FCSTD DOCUMENT  (FreeCAD 0.19R22665 (Git))
Label: assembly
License: All rights reserved
LicenseURL: http://en.wikipedia.org/wiki/All_rights_reserved
objects: App::Link×5, App::DocumentObjectGroup×2, PartDesign::CoordinateSystem×1, App::FeaturePython×1, App::Part×1
note: 1 computed .brp shape members not serialized (recipe doc carries the construction recipe); baked Part::Feature solids carry a one-line shape summary decoded from their .brp
EXTERNAL_REF file=box_part.FCStd obj=LCS_backplane
EXTERNAL_REF file=box_part.FCStd obj=Body
EXTERNAL_REF file=box_part.FCStd obj=LCS_pcb
EXTERNAL_REF file=pcb_board.FCStd obj=LCS_box
EXTERNAL_REF file=pcb_board.FCStd obj=Board_8929
EXTERNAL_REF file=lcd.FCStd obj=LCS_pcb
EXTERNAL_REF file=pcb_board.FCStd obj=LCS_lcd
EXTERNAL_REF file=lcd.FCStd obj=Part
EXTERNAL_REF file=box_part.FCStd obj=LCS_coperchio
EXTERNAL_REF file=coperchio.FCStd obj=LCS_box
EXTERNAL_REF file=coperchio.FCStd obj=Part
EXTERNAL_REF file=coperchio.FCStd obj=LCS_button
EXTERNAL_REF file=push_button.FCStd obj=LCS_coperchio
EXTERNAL_REF file=push_button.FCStd obj=Part

FEATURE [App::DocumentObjectGroup] Parts
FEATURE [PartDesign::CoordinateSystem] LCS_Origin
  AttacherType = Attacher::AttachEngine3D
  MapMode = 2
  Support = -> [X_Axis]
FEATURE [App::DocumentObjectGroup] Constraints
FEATURE [App::FeaturePython] Variables  # WARN: FeaturePython — macro-defined, semantics opaque (R4)
FEATURE [App::Link] box_part_box
  AssemblyType = Asm4EE
  AttachedBy = #LCS_backplane
  AttachedTo = Parent Assembly#LCS_Origin
  AttachmentOffset = pos=(0,0,0) rot=(0,0.707107,0.707107;3.14159rad)
  LinkPlacement = pos=(1e-16,2,-4e-16) rot=(0,0,1;0rad)
  LinkedObject = -> <external box_part.FCStd>#Body
  Placement = pos=(1e-16,2,-4e-16) rot=(0,0,1;0rad)
  expr: Placement = LCS_Origin.Placement * AttachmentOffset * box_part#LCS_backplane.Placement ^ -1
FEATURE [App::Link] pcb_board_livello_serbatoio_definitiva
  AssemblyType = Asm4EE
  AttachedBy = #LCS_box
  AttachedTo = box_part_box#LCS_pcb
  LinkPlacement = pos=(-68.25,-39.4,154) rot=(1,0,0;1.5708rad)
  LinkedObject = -> <external pcb_board.FCStd>#Board_8929
  Placement = pos=(-68.25,-39.4,154) rot=(1,0,0;1.5708rad)
  expr: Placement = box_part_box.Placement * box_part#LCS_pcb.Placement * AttachmentOffset * pcb_board#LCS_box.Placement ^ -1
FEATURE [App::Link] lcd_lcd_block
  AssemblyType = Asm4EE
  AttachedBy = #LCS_pcb
  AttachedTo = pcb_board_livello_serbatoio_definitiva#LCS_lcd
  LinkPlacement = pos=(100.73,-48.9,32.02) rot=(1,0,0;1.5708rad)
  LinkedObject = -> <external lcd.FCStd>#Part
  Placement = pos=(100.73,-48.9,32.02) rot=(1,0,0;1.5708rad)
  expr: Placement = pcb_board_livello_serbatoio_definitiva.Placement * pcb_board#LCS_lcd.Placement * AttachmentOffset * lcd#LCS_pcb.Placement ^ -1
FEATURE [App::Link] coperchio_coperchio_completo
  AssemblyType = Asm4EE
  AttachedBy = #LCS_box
  AttachedTo = box_part_box#LCS_coperchio
  LinkPlacement = pos=(4e-15,-13,2.13e-14) rot=(0,0,1;0rad)
  LinkedObject = -> <external coperchio.FCStd>#Part
  Placement = pos=(4e-15,-13,2.13e-14) rot=(0,0,1;0rad)
  expr: Placement = box_part_box.Placement * box_part#LCS_coperchio.Placement * AttachmentOffset * coperchio#LCS_box.Placement ^ -1
FEATURE [App::Link] push_button_push_button_complete
  AssemblyType = Asm4EE
  AttachedBy = #LCS_coperchio
  AttachedTo = coperchio_coperchio_completo#LCS_button
  AttachmentOffset = pos=(0,0,0) rot=(-1,0,0;3.14159rad)
  LinkPlacement = pos=(121.75,-60,50) rot=(0,-1,0;3.14159rad)
  LinkedObject = -> <external push_button.FCStd>#Part
  Placement = pos=(121.75,-60,50) rot=(0,-1,0;3.14159rad)
  expr: Placement = coperchio_coperchio_completo.Placement * coperchio#LCS_button.Placement * AttachmentOffset * push_button#LCS_coperchio.Placement ^ -1
FEATURE [App::Part] Model
  Configuration = 0
  Group = -> [LCS_Origin,Constraints,Variables,box_part_box,pcb_board_livello_serbatoio_definitiva,lcd_lcd_block,coperchio_coperchio_completo,push_button_push_button_complete]
  Origin = -> Origin
  Type = Assembly4 Model

RESOLVED EXTERNAL PARTS (link-assembly join: the EXTERNAL_REF files above that resolve inside this repo's crawl, each included once):
---- part box_part.FCStd = doc fcstd_5c013ba1774b ----
FCSTD DOCUMENT  (FreeCAD 0.19R22665 (Git))
Label: box_part
License: All rights reserved
LicenseURL: http://en.wikipedia.org/wiki/All_rights_reserved
objects: Sketcher::SketchObject×9, PartDesign::Pocket×6, PartDesign::Pad×3, PartDesign::CoordinateSystem×3, PartDesign::Fillet×2, PartDesign::Chamfer×1, PartDesign::Body×1
note: 37 computed .brp shape members not serialized (recipe doc carries the construction recipe); baked Part::Feature solids carry a one-line shape summary decoded from their .brp

FEATURE [Sketcher::SketchObject] Sketch
  MapMode = 5
  Placement = pos=(0,0,0) rot=(1,0,0;1.5708rad)
  Support = -> [XZ_Plane]
  sketch-geometry (4):
    g0: LineSegment StartX=0 StartY=0 StartZ=0 EndX=150 EndY=0 EndZ=0
    g1: LineSegment StartX=150 StartY=0 StartZ=0 EndX=150 EndY=100 EndZ=0
    g2: LineSegment StartX=150 StartY=100 StartZ=0 EndX=0 EndY=100 EndZ=0
    g3: LineSegment StartX=0 StartY=100 StartZ=0 EndX=0 EndY=0 EndZ=0
  constraints (11):
    c: Coincident(g0,g1)
    c: Coincident(g1,g2)
    c: Coincident(g2,g3)
    c: Coincident(g3,g0)
    c: Horizontal(g0)
    c: Horizontal(g2)
    c: Vertical(g1)
    c: Vertical(g3)
    c: Coincident(g0,g-1)
    c: Distance(g2) = 150
    c: Distance(g3) = 100
FEATURE [PartDesign::Pad] Pad
  Direction = (1,1,1)
  Length = 60
  Length2 = 100
  Placement = pos=(0,0,0) rot=(1,0,0;1.5708rad)
  Profile = -> Sketch
  Type = 0
FEATURE [Sketcher::SketchObject] Sketch001
  ExternalGeometry = -> [Pad]
  MapMode = 5
  Placement = pos=(0,-60,-1.32e-14) rot=(1,0,0;1.5708rad)
  Support = -> [Pad]
  sketch-geometry (13):
    g0: LineSegment StartX=2 StartY=98 StartZ=0 EndX=148 EndY=98 EndZ=0
    g1: LineSegment StartX=148 StartY=98 StartZ=0 EndX=148 EndY=56 EndZ=0
    g2: LineSegment StartX=148 StartY=56 StartZ=0 EndX=142 EndY=56 EndZ=0
    g3: LineSegment StartX=142 StartY=56 StartZ=0 EndX=142 EndY=44 EndZ=0
    g4: LineSegment StartX=142 StartY=44 StartZ=0 EndX=148 EndY=44 EndZ=0
    g5: LineSegment StartX=148 StartY=44 StartZ=0 EndX=148 EndY=2 EndZ=0
    g6: LineSegment StartX=148 StartY=2 StartZ=0 EndX=2 EndY=2 EndZ=0
    g7: LineSegment StartX=2 StartY=2 StartZ=0 EndX=2 EndY=44 EndZ=0
    g8: LineSegment StartX=2 StartY=44 StartZ=0 EndX=8 EndY=44 EndZ=0
    g9: LineSegment StartX=8 StartY=44 StartZ=0 EndX=8 EndY=56 EndZ=0
    g10: LineSegment StartX=8 StartY=56 StartZ=0 EndX=2 EndY=56 EndZ=0
    g11: LineSegment StartX=2 StartY=56 StartZ=0 EndX=2 EndY=98 EndZ=0
    g12: LineSegment [constr] StartX=0 StartY=50 StartZ=0 EndX=150 EndY=50 EndZ=0
  constraints (37):
    c: Horizontal(g0)
    c: Coincident(g0,g1)
    c: Vertical(g1)
    c: Coincident(g1,g2)
    c: Horizontal(g2)
    c: Coincident(g2,g3)
    c: Vertical(g3)
    c: Coincident(g3,g4)
    c: Horizontal(g4)
    c: Coincident(g4,g5)
    c: Vertical(g5)
    c: Coincident(g5,g6)
    c: Horizontal(g6)
    c: Coincident(g6,g7)
    c: Vertical(g7)
    c: Coincident(g7,g8)
    c: Horizontal(g8)
    c: Coincident(g8,g9)
    c: Vertical(g9)
    c: Coincident(g9,g10)
    c: Horizontal(g10)
    c: Coincident(g10,g11)
    c: Coincident(g11,g0)
    c: Vertical(g11)
    c: DistanceX(g-1,g6) = 2
    c: DistanceY(g-1,g6) = 2
    c: DistanceX(g5,g-5) = 2
    c: DistanceY(g0,g-6) = 2
    c: PointOnObject(g12,g-4)
    c: PointOnObject(g12,g-5)
    c: Symmetric(g-6,g-1,g12)
    c: Symmetric(g10,g7,g12)
    c: DistanceX(g10,g10) = 6
    c: DistanceY(g9,g9) = 12
    c: Equal(g2,g10)
    c: Equal(g3,g9)
    c: Symmetric(g1,g4,g12)
FEATURE [PartDesign::Pocket] Pocket
  BaseFeature = -> Pad
  Length = 58
  Length2 = 100
  Placement = pos=(0,0,0) rot=(1,0,0;1.5708rad)
  Profile = -> Sketch001
  Type = 0
FEATURE [Sketcher::SketchObject] Sketch002
  ExternalGeometry = -> [Pocket]
  MapMode = 5
  Placement = pos=(0,-2,-4e-16) rot=(1,0,0;1.5708rad)
  Support = -> [Pocket]
  sketch-geometry (20):
    g0: LineSegment [constr] StartX=20.75 StartY=68 StartZ=0 EndX=100.75 EndY=68 EndZ=0
    g1: LineSegment [constr] StartX=100.75 StartY=68 StartZ=0 EndX=100.75 EndY=32 EndZ=0
    g2: LineSegment [constr] StartX=100.75 StartY=32 StartZ=0 EndX=20.75 EndY=32 EndZ=0
    g3: LineSegment [constr] StartX=20.75 StartY=32 StartZ=0 EndX=20.75 EndY=68 EndZ=0
    g4: LineSegment [constr] StartX=8 StartY=50 StartZ=0 EndX=142 EndY=50 EndZ=0
    g5: Circle [constr] CenterX=121.75 CenterY=50 CenterZ=0 NormalX=0 NormalY=0 NormalZ=1 AngleXU=0 Radius=9.5
    g6: LineSegment [constr] StartX=101.75 StartY=14 StartZ=0 EndX=18.75 EndY=14 EndZ=0
    g7: LineSegment [constr] StartX=18.75 StartY=14 StartZ=0 EndX=18.75 EndY=86 EndZ=0
    g8: LineSegment [constr] StartX=18.75 StartY=86 StartZ=0 EndX=101.75 EndY=86 EndZ=0
    g9: LineSegment [constr] StartX=101.75 StartY=86 StartZ=0 EndX=101.75 EndY=14 EndZ=0
    g10: LineSegment [constr] StartX=101.75 StartY=59 StartZ=0 EndX=107.75 EndY=59 EndZ=0
    g11: LineSegment [constr] StartX=107.75 StartY=59 StartZ=0 EndX=107.75 EndY=72 EndZ=0
    g12: LineSegment [constr] StartX=107.75 StartY=72 StartZ=0 EndX=101.75 EndY=72 EndZ=0
    g13: LineSegment [constr] StartX=101.75 StartY=72 StartZ=0 EndX=101.75 EndY=59 EndZ=0
    g14: Circle [constr] CenterX=13.375 CenterY=50 CenterZ=0 NormalX=0 NormalY=0 NormalZ=1 AngleXU=0 Radius=5.375
    g15: Circle [constr] CenterX=136.625 CenterY=50 CenterZ=0 NormalX=0 NormalY=0 NormalZ=1 AngleXU=0 Radius=5.375
    g16: Circle CenterX=24.75 CenterY=80 CenterZ=0 NormalX=0 NormalY=0 NormalZ=1 AngleXU=0 Radius=3
    g17: Circle CenterX=95.75 CenterY=80 CenterZ=0 NormalX=0 NormalY=0 NormalZ=1 AngleXU=0 Radius=3
    g18: Circle CenterX=24.75 CenterY=20 CenterZ=0 NormalX=0 NormalY=0 NormalZ=1 AngleXU=0 Radius=3
    g19: Circle CenterX=95.75 CenterY=20 CenterZ=0 NormalX=0 NormalY=0 NormalZ=1 AngleXU=0 Radius=3
  constraints (59):
    c: Coincident(g0,g1)
    c: Coincident(g1,g2)
    c: Coincident(g2,g3)
    c: Coincident(g3,g0)
    c: Horizontal(g0)
    c: Horizontal(g2)
    c: Vertical(g1)
    c: DistanceY(g3,g3) = 36
    c: DistanceX(g0,g0) = 80
    c: PointOnObject(g4,g-13)
    c: PointOnObject(g4,g-11)
    c: Symmetric(g-13,g-14,g4)
    c: Symmetric(g0,g2,g4)
    c: PointOnObject(g5,g4)
    c: Diameter(g5) = 19
    c: Coincident(g6,g7)
    c: Coincident(g7,g8)
    c: Coincident(g8,g9)
    c: Coincident(g9,g6)
    c: Horizontal(g6)
    c: Horizontal(g8)
    c: Vertical(g7)
    c: Vertical(g9)
    c: DistanceX(g6,g2) = 2
    c: DistanceY(g0,g7) = 18
    c: DistanceY(g6,g2) = 18
    c: DistanceX(g8,g8) = 83
    c: Coincident(g10,g11)
    c: Coincident(g11,g12)
    c: Coincident(g12,g13)
    c: Coincident(g13,g10)
    c: Horizontal(g10)
    c: Horizontal(g12)
    c: Vertical(g11)
    c: Vertical(g13)
    c: PointOnObject(g10,g9)
    c: DistanceY(g11,g11) = 13
    c: DistanceY(g12,g8) = 14
    c: DistanceX(g12,g12) = 6
    c: DistanceX(g6,g5) = 20
    c: PointOnObject(g14,g4)
    c: PointOnObject(g4,g14)
    c: Tangent(g14,g7)
    c: PointOnObject(g15,g4)
    c: PointOnObject(g4,g15)
    c: Tangent(g15,g5)
    c: Equal(g15,g14)
    c: DistanceX(g7,g16) = 6
    c: DistanceY(g16,g7) = 6
    c: Diameter(g16) = 6
    c: Horizontal(g17,g16)
    c: Equal(g17,g16)
    c: DistanceX(g17,g8) = 6
    c: Equal(g18,g16)
    c: Vertical(g16,g18)
    c: DistanceY(g6,g18) = 6
    c: Equal(g19,g16)
    c: Horizontal(g19,g18)
    c: Vertical(g17,g19)
FEATURE [PartDesign::Pad] Pad001
  BaseFeature = -> Pocket
  Direction = (1,1,1)
  Length = 37.8
  Length2 = 100
  Placement = pos=(0,0,0) rot=(1,0,0;1.5708rad)
  Profile = -> Sketch002
  Type = 0
FEATURE [Sketcher::SketchObject] Sketch005
  MapMode = 5
  Placement = pos=(0,0,0) rot=(1,0,0;3.14159rad)
  sketch-geometry (5):
    g0: LineSegment [constr] StartX=75 StartY=60 StartZ=0 EndX=75 EndY=0 EndZ=0
    g1: ArcOfCircle CenterX=65 CenterY=9 CenterZ=0 NormalX=0 NormalY=0 NormalZ=1 AngleXU=0 Radius=4 StartAngle=1.5708 EndAngle=4.71239
    g2: ArcOfCircle CenterX=85 CenterY=9 CenterZ=0 NormalX=0 NormalY=0 NormalZ=1 AngleXU=0 Radius=4 StartAngle=4.71239 EndAngle=7.85398
    g3: LineSegment StartX=65 StartY=5 StartZ=0 EndX=85 EndY=5 EndZ=0
    g4: LineSegment StartX=65 StartY=13 StartZ=0 EndX=85 EndY=13 EndZ=0
  constraints (9):
    c: Tangent(g1,g4)
    c: Tangent(g1,g3)
    c: Tangent(g3,g2)
    c: Tangent(g4,g2)
    c: Horizontal(g3)
    c: DistanceX(g1,g2) = 20
    c: DistanceY(g1,g1) = 8
    c: Symmetric(g2,g1,g0)
    c: DistanceY(g0,g2) = 5
FEATURE [PartDesign::Pocket] Pocket001
  BaseFeature = -> Pad001
  Length = 5
  Length2 = 100
  Placement = pos=(0,0,0) rot=(1,0,0;1.5708rad)
  Profile = -> Sketch005
  Type = 2
FEATURE [Sketcher::SketchObject] Sketch006
  ExternalGeometry = -> [Pocket001]
  MapMode = 5
  Placement = pos=(150,0,0) rot=(0.707107,0,0.707107;3.14159rad)
  Support = -> [Pocket001]
  sketch-geometry (5):
    g0: LineSegment [constr] StartX=0 StartY=30 StartZ=0 EndX=2 EndY=30 EndZ=0
    g1: ArcOfCircle CenterX=17.5 CenterY=35 CenterZ=0 NormalX=0 NormalY=0 NormalZ=1 AngleXU=0 Radius=7.5 StartAngle=1e-16 EndAngle=3.14159
    g2: ArcOfCircle CenterX=17.5 CenterY=25 CenterZ=0 NormalX=0 NormalY=0 NormalZ=1 AngleXU=0 Radius=7.5 StartAngle=3.14159 EndAngle=6.28319
    g3: LineSegment StartX=10 StartY=35 StartZ=0 EndX=10 EndY=25 EndZ=0
    g4: LineSegment StartX=25 StartY=35 StartZ=0 EndX=25 EndY=25 EndZ=0
  constraints (12):
    c: PointOnObject(g0,g-6)
    c: PointOnObject(g0,g-4)
    c: Symmetric(g-6,g-1,g0)
    c: Tangent(g1,g4)
    c: Tangent(g1,g3)
    c: Tangent(g3,g2)
    c: Tangent(g4,g2)
    c: Vertical(g3)
    c: Symmetric(g1,g2,g0)
    c: DistanceX(g1,g1) = 15
    c: Distance(g1,g2) = 10
    c: DistanceX(g-6,g1) = 10
FEATURE [PartDesign::Pocket] Pocket002
  BaseFeature = -> Pocket001
  Length = 5
  Length2 = 100
  Placement = pos=(0,0,0) rot=(1,0,0;1.5708rad)
  Profile = -> Sketch006
  Type = 2
FEATURE [Sketcher::SketchObject] Sketch007
  ExternalGeometry = -> [Pocket002]
  MapMode = 5
  Placement = pos=(0,-2,-4e-16) rot=(1,0,0;1.5708rad)
  Support = -> [Pocket002]
  sketch-geometry (4):
    g0: Circle CenterX=40 CenterY=50 CenterZ=0 NormalX=0 NormalY=0 NormalZ=1 AngleXU=0 Radius=1
    g1: Circle CenterX=110 CenterY=50 CenterZ=0 NormalX=0 NormalY=0 NormalZ=1 AngleXU=0 Radius=1
    g2: LineSegment [constr] StartX=8 StartY=50 StartZ=0 EndX=142 EndY=50 EndZ=0
    g3: LineSegment [constr] StartX=75 StartY=98 StartZ=0 EndX=75 EndY=2 EndZ=0
  constraints (11):
    c: Diameter(g0) = 2
    c: Equal(g1,g0)
    c: DistanceX(g0,g1) = 70
    c: PointOnObject(g2,g-3)
    c: PointOnObject(g2,g-4)
    c: Symmetric(g-4,g-4,g2)
    c: PointOnObject(g0,g2)
    c: PointOnObject(g3,g-5)
    c: PointOnObject(g3,g-6)
    c: Symmetric(g-5,g-5,g3)
    c: Symmetric(g0,g1,g3)
FEATURE [PartDesign::Pocket] Pocket003
  BaseFeature = -> Pocket002
  Length = 2
  Length2 = 100
  Placement = pos=(0,0,0) rot=(1,0,0;1.5708rad)
  Profile = -> Sketch007
  Type = 1
FEATURE [Sketcher::SketchObject] Sketch009
  ExternalGeometry = -> [Pocket003]
  MapMode = 5
  Placement = pos=(-2e-15,-39.8,-1.03e-14) rot=(1,0,0;1.5708rad)
  Support = -> [Pocket003]
  sketch-geometry (4):
    g0: Circle CenterX=24.75 CenterY=80 CenterZ=0 NormalX=0 NormalY=0 NormalZ=1 AngleXU=0 Radius=1.5
    g1: Circle CenterX=95.75 CenterY=80 CenterZ=0 NormalX=0 NormalY=0 NormalZ=1 AngleXU=0 Radius=1.5
    g2: Circle CenterX=24.75 CenterY=20 CenterZ=0 NormalX=0 NormalY=0 NormalZ=1 AngleXU=0 Radius=1.5
    g3: Circle CenterX=95.75 CenterY=20 CenterZ=0 NormalX=0 NormalY=0 NormalZ=1 AngleXU=0 Radius=1.5
  constraints (8):
    c: Coincident(g0,g-3)
    c: Coincident(g1,g-4)
    c: Coincident(g2,g-6)
    c: Coincident(g3,g-5)
    c: Diameter(g0) = 3
    c: Equal(g1,g0)
    c: Equal(g2,g0)
    c: Equal(g2,g3)
FEATURE [PartDesign::Pad] Pad003
  BaseFeature = -> Pocket003
  Direction = (1,1,1)
  Length = 10
  Length2 = 100
  Placement = pos=(0,0,0) rot=(1,0,0;1.5708rad)
  Profile = -> Sketch009
  Type = 0
FEATURE [Sketcher::SketchObject] Sketch010
  ExternalGeometry = -> [Pad003]
  MapMode = 5
  Placement = pos=(0,-1.85e-14,56) rot=(0,0,1;3.14159rad)
  Support = -> [Pad003]
  sketch-geometry (18):
    g0: LineSegment StartX=-3.75 StartY=60 StartZ=0 EndX=-3.75 EndY=57.3 EndZ=0
    g1: LineSegment StartX=-3.75 StartY=57.3 StartZ=0 EndX=-2.75 EndY=57.3 EndZ=0
    g2: LineSegment StartX=-2.75 StartY=57.3 StartZ=0 EndX=-2.75 EndY=51.7 EndZ=0
    g3: LineSegment StartX=-2.75 StartY=51.7 StartZ=0 EndX=-7.25 EndY=51.7 EndZ=0
    g4: LineSegment StartX=-7.25 StartY=51.7 StartZ=0 EndX=-7.25 EndY=57.3 EndZ=0
    g5: LineSegment StartX=-7.25 StartY=57.3 StartZ=0 EndX=-6.25 EndY=57.3 EndZ=0
    g6: LineSegment StartX=-6.25 StartY=57.3 StartZ=0 EndX=-6.25 EndY=60 EndZ=0
    g7: LineSegment StartX=-6.25 StartY=60 StartZ=0 EndX=-3.75 EndY=60 EndZ=0
    g8: LineSegment [constr] StartX=-2 StartY=50 StartZ=0 EndX=-8 EndY=50 EndZ=0
    g9: LineSegment [constr] StartX=-5 StartY=50 StartZ=0 EndX=-5 EndY=60 EndZ=0
    g10: LineSegment [constr] StartX=-6 StartY=60 StartZ=0 EndX=-4 EndY=60 EndZ=0
    g11: LineSegment [constr] StartX=-4 StartY=60 StartZ=0 EndX=-4 EndY=52 EndZ=0
    g12: LineSegment [constr] StartX=-4 StartY=52 StartZ=0 EndX=-6 EndY=52 EndZ=0
    g13: LineSegment [constr] StartX=-6 StartY=52 StartZ=0 EndX=-6 EndY=60 EndZ=0
    g14: LineSegment [constr] StartX=-7 StartY=52 StartZ=0 EndX=-3 EndY=52 EndZ=0
    g15: LineSegment [constr] StartX=-3 StartY=52 StartZ=0 EndX=-3 EndY=57 EndZ=0
    g16: LineSegment [constr] StartX=-3 StartY=57 StartZ=0 EndX=-7 EndY=57 EndZ=0
    g17: LineSegment [constr] StartX=-7 StartY=57 StartZ=0 EndX=-7 EndY=52 EndZ=0
  constraints (52):
    c: PointOnObject(g0,g-3)
    c: Vertical(g0)
    c: Coincident(g0,g1)
    c: Coincident(g1,g2)
    c: Vertical(g2)
    c: Coincident(g2,g3)
    c: Horizontal(g3)
    c: Coincident(g3,g4)
    c: Vertical(g4)
    c: Coincident(g4,g5)
    c: Horizontal(g5)
    c: Coincident(g5,g6)
    c: PointOnObject(g6,g-3)
    c: Vertical(g6)
    c: Coincident(g6,g7)
    c: Coincident(g7,g0)
    c: DistanceX(g6,g0) = 2.5
    c: DistanceX(g1,g1) = 1
    c: DistanceY(g4,g4) = 5.6
    c: Horizontal(g1)
    c: DistanceY(g6,g6) = 2.7
    c: PointOnObject(g8,g-5)
    c: Horizontal(g8)
    c: PointOnObject(g9,g8)
    c: Symmetric(g-5,g-4,g9)
    c: Symmetric(g0,g5,g9)
    c: DistanceY(g8,g-4) = 10
    c: PointOnObject(g9,g7)
    c: PointOnObject(g8,g-4)
    c: Equal(g1,g5)
    c: Coincident(g10,g11)
    c: Coincident(g11,g12)
    c: Coincident(g12,g13)
    c: Coincident(g13,g10)
    c: Horizontal(g12)
    c: Vertical(g11)
    c: Vertical(g13)
    c: PointOnObject(g10,g7)
    c: Symmetric(g10,g10,g9)
    c: DistanceX(g12,g12) = 2
    c: DistanceY(g13,g13) = 8
    c: Coincident(g14,g15)
    c: Coincident(g15,g16)
    c: Coincident(g16,g17)
    c: Coincident(g17,g14)
    c: Horizontal(g14)
    c: Vertical(g15)
    c: Vertical(g17)
    c: DistanceX(g16,g16) = 4
    c: Symmetric(g15,g16,g9)
    c: DistanceY(g15,g10) = 3
    c: DistanceY(g11,g14) = 0
FEATURE [PartDesign::Pocket] Pocket004
  BaseFeature = -> Pad003
  Length = 6
  Length2 = 100
  Placement = pos=(0,0,0) rot=(1,0,0;1.5708rad)
  Profile = -> Sketch010
  Type = 0
FEATURE [Sketcher::SketchObject] Sketch011
  ExternalGeometry = -> [Pocket004]
  MapMode = 5
  Placement = pos=(0,-1.85e-14,56) rot=(0,0,1;3.14159rad)
  Support = -> [Pocket004]
  sketch-geometry (9):
    g0: LineSegment StartX=-143.75 StartY=60 StartZ=0 EndX=-146.25 EndY=60 EndZ=0
    g1: LineSegment StartX=-146.25 StartY=60 StartZ=0 EndX=-146.25 EndY=57.3 EndZ=0
    g2: LineSegment StartX=-146.25 StartY=57.3 StartZ=0 EndX=-147.25 EndY=57.3 EndZ=0
    g3: LineSegment StartX=-147.25 StartY=57.3 StartZ=0 EndX=-147.25 EndY=51.7 EndZ=0
    g4: LineSegment StartX=-147.25 StartY=51.7 StartZ=0 EndX=-142.75 EndY=51.7 EndZ=0
    g5: LineSegment StartX=-142.75 StartY=51.7 StartZ=0 EndX=-142.75 EndY=57.3 EndZ=0
    g6: LineSegment StartX=-142.75 StartY=57.3 StartZ=0 EndX=-143.75 EndY=57.3 EndZ=0
    g7: LineSegment StartX=-143.75 StartY=57.3 StartZ=0 EndX=-143.75 EndY=60 EndZ=0
    g8: LineSegment [constr] StartX=-145 StartY=51.7 StartZ=0 EndX=-145 EndY=60 EndZ=0
  constraints (26):
    c: PointOnObject(g0,g-3)
    c: PointOnObject(g0,g-3)
    c: Coincident(g0,g1)
    c: Vertical(g1)
    c: Coincident(g1,g2)
    c: Coincident(g2,g3)
    c: Vertical(g3)
    c: Coincident(g3,g4)
    c: Horizontal(g4)
    c: Coincident(g4,g5)
    c: Coincident(g5,g6)
    c: Coincident(g6,g7)
    c: Coincident(g7,g0)
    c: Equal(g5,g3)
    c: Equal(g2,g6)
    c: Equal(g7,g1)
    c: Vertical(g7)
    c: DistanceX(g0,g0) = 2.5
    c: Horizontal(g6)
    c: DistanceX(g6,g6) = 1
    c: DistanceY(g7,g7) = 2.7
    c: DistanceY(g5,g5) = 5.6
    c: PointOnObject(g8,g4)
    c: PointOnObject(g8,g0)
    c: Symmetric(g-4,g-5,g8)
    c: Symmetric(g5,g2,g8)
FEATURE [PartDesign::Pocket] Pocket005
  BaseFeature = -> Pocket004
  Length = 6
  Length2 = 100
  Placement = pos=(0,0,0) rot=(1,0,0;1.5708rad)
  Profile = -> Sketch011
  Type = 0
FEATURE [PartDesign::Chamfer] Chamfer
  Angle = 60
  Base = -> Pocket005 [Edge120,Edge122,Edge121,Edge119]
  BaseFeature = -> Pocket005
  ChamferType = 2
  FlipDirection = false
  Placement = pos=(0,0,0) rot=(1,0,0;1.5708rad)
  Size = 4
  Size2 = 1
  SupportTransform = false
FEATURE [PartDesign::Fillet] Fillet
  Base = -> Chamfer [Edge21,Edge56,Edge59,Edge23]
  BaseFeature = -> Chamfer
  Placement = pos=(0,0,0) rot=(1,0,0;1.5708rad)
  Radius = 2
  SupportTransform = false
FEATURE [PartDesign::Fillet] Fillet001
  Base = -> Fillet [Edge155,Edge157,Edge158,Edge156]
  BaseFeature = -> Fillet
  Placement = pos=(0,0,0) rot=(1,0,0;1.5708rad)
  Radius = 2
  SupportTransform = false
FEATURE [PartDesign::CoordinateSystem] LCS_backplane
  AttacherType = Attacher::AttachEngine3D
  MapMode = 5
  Placement = pos=(0,-2,-4e-16) rot=(0,0.707107,0.707107;3.14159rad)
  Support = -> [Fillet001]
FEATURE [PartDesign::CoordinateSystem] LCS_pcb
  AttacherType = Attacher::AttachEngine3D
  MapMode = 11
  Placement = pos=(24.75,-39.8,20) rot=(0.57735,-0.57735,0.57735;2.0944rad)
  Support = -> [Fillet001]
FEATURE [PartDesign::CoordinateSystem] LCS_coperchio
  AttacherType = Attacher::AttachEngine3D
  AttachmentOffset = pos=(0.3,0,-0.25) rot=(0,0,1;0rad)
  MapMode = 7
  Placement = pos=(3,-52,50) rot=(0.57735,-0.57735,-0.57735;2.0944rad)
  Support = -> [Fillet001]
FEATURE [PartDesign::Body] Body  label="box"
  Group = -> [Sketch,Pad,Sketch001,Pocket,Sketch002,Pad001,Sketch005,Pocket001,Sketch006,Pocket002,Sketch007,LCS_backplane,LCS_pcb,LCS_coperchio,Pocket003,Sketch009,Pad003,Sketch010,Pocket004,Sketch011,Pocket005,Chamfer,Fillet,Fillet001]
  Origin = -> Origin
  Tip = -> Fillet001
---- part coperchio.FCStd = doc fcstd_1bf6bf9a385b ----
FCSTD DOCUMENT  (FreeCAD 0.19R22665 (Git))
Label: coperchio
License: All rights reserved
LicenseURL: http://en.wikipedia.org/wiki/All_rights_reserved
objects: Sketcher::SketchObject×7, PartDesign::Pocket×5, PartDesign::Pad×3, PartDesign::CoordinateSystem×2, PartDesign::Body×2, Part::Fillet×2, Part::Part2DObjectPython×1, Part::Extrusion×1, Part::MultiFuse×1, App::Part×1
note: 32 computed .brp shape members not serialized (recipe doc carries the construction recipe); baked Part::Feature solids carry a one-line shape summary decoded from their .brp

FEATURE [Part::Part2DObjectPython] ShapeString  # Draft 2D object (typed FeaturePython)
  FontFile = <path>
  Placement = pos=(111.263,-47,22.0884) rot=(1,0,0;1.5708rad)
  Size = 2
  String = by GR 2021
  Tracking = 0
FEATURE [Part::Extrusion] Extrude002
  Base = -> ShapeString
  Dir = (0,-1,2e-16)
  DirMode = 2
  FaceMakerClass = Part::FaceMakerBullseye
  LengthFwd = 1
  LengthRev = 0
  Placement = pos=(21,0,-19) rot=(0,0,1;0rad)
  Solid = false
  Symmetric = false
FEATURE [Sketcher::SketchObject] Sketch008
  MapMode = 5
  Placement = pos=(0,-45,1e-16) rot=(1,0,0;1.5708rad)
  sketch-geometry (4):
    g0: LineSegment StartX=0 StartY=0 StartZ=0 EndX=150 EndY=0 EndZ=0
    g1: LineSegment StartX=150 StartY=0 StartZ=0 EndX=150 EndY=100 EndZ=0
    g2: LineSegment StartX=150 StartY=100 StartZ=0 EndX=0 EndY=100 EndZ=0
    g3: LineSegment StartX=0 StartY=100 StartZ=0 EndX=0 EndY=0 EndZ=0
  constraints (11):
    c: Coincident(g0,g1)
    c: Coincident(g1,g2)
    c: Coincident(g2,g3)
    c: Coincident(g3,g0)
    c: Horizontal(g0)
    c: Horizontal(g2)
    c: Vertical(g1)
    c: Vertical(g3)
    c: Coincident(g0,g-1)
    c: DistanceY(g0,g2) = 100
    c: DistanceX(g0,g0) = 150
FEATURE [PartDesign::Pad] Pad002
  Direction = (1,1,1)
  Length = 2
  Length2 = 100
  Placement = pos=(0,-45,1e-16) rot=(1,0,0;1.5708rad)
  Profile = -> Sketch008
  Type = 0
FEATURE [Sketcher::SketchObject] Sketch009
  ExternalGeometry = -> [Pad002]
  MapMode = 5
  Placement = pos=(0,-47,5e-16) rot=(1,0,0;1.5708rad)
  Support = -> [Pad002]
  sketch-geometry (22):
    g0: LineSegment StartX=23.75 StartY=64 StartZ=0 EndX=97.75 EndY=64 EndZ=0
    g1: LineSegment StartX=97.75 StartY=64 StartZ=0 EndX=97.75 EndY=36 EndZ=0
    g2: LineSegment StartX=97.75 StartY=36 StartZ=0 EndX=23.75 EndY=36 EndZ=0
    g3: LineSegment StartX=23.75 StartY=36 StartZ=0 EndX=23.75 EndY=64 EndZ=0
    g4: LineSegment [constr] StartX=18.75 StartY=86 StartZ=0 EndX=101.75 EndY=86 EndZ=0
    g5: LineSegment [constr] StartX=101.75 StartY=86 StartZ=0 EndX=101.75 EndY=14 EndZ=0
    g6: LineSegment [constr] StartX=101.75 StartY=14 StartZ=0 EndX=18.75 EndY=14 EndZ=0
    g7: LineSegment [constr] StartX=18.75 StartY=14 StartZ=0 EndX=18.75 EndY=86 EndZ=0
    g8: Circle CenterX=121.75 CenterY=50 CenterZ=0 NormalX=0 NormalY=0 NormalZ=1 AngleXU=0 Radius=9.5
    g9: LineSegment [constr] StartX=20.75 StartY=68 StartZ=0 EndX=100.75 EndY=68 EndZ=0
    g10: LineSegment [constr] StartX=100.75 StartY=68 StartZ=0 EndX=100.75 EndY=32 EndZ=0
    g11: LineSegment [constr] StartX=100.75 StartY=32 StartZ=0 EndX=20.75 EndY=32 EndZ=0
    g12: LineSegment [constr] StartX=20.75 StartY=32 StartZ=0 EndX=20.75 EndY=68 EndZ=0
    g13: LineSegment [constr] StartX=0 StartY=50 StartZ=0 EndX=150 EndY=50 EndZ=0
    g14: LineSegment [constr] StartX=60.75 StartY=68 StartZ=0 EndX=60.75 EndY=32 EndZ=0
    g15: Circle [constr] CenterX=9.375 CenterY=50 CenterZ=0 NormalX=0 NormalY=0 NormalZ=1 AngleXU=0 Radius=9.375
    g16: Circle [constr] CenterX=140.625 CenterY=50 CenterZ=0 NormalX=0 NormalY=0 NormalZ=1 AngleXU=0 Radius=9.375
    g17: ArcOfCircle CenterX=68.1 CenterY=80.85 CenterZ=0 NormalX=0 NormalY=0 NormalZ=1 AngleXU=0 Radius=3.25 StartAngle=1.5708 EndAngle=4.71239
    g18: ArcOfCircle CenterX=81.6 CenterY=80.85 CenterZ=0 NormalX=0 NormalY=0 NormalZ=1 AngleXU=0 Radius=3.25 StartAngle=4.71239 EndAngle=7.85398
    g19: LineSegment StartX=68.1 StartY=77.6 StartZ=0 EndX=81.6 EndY=77.6 EndZ=0
    g20: LineSegment StartX=68.1 StartY=84.1 StartZ=0 EndX=81.6 EndY=84.1 EndZ=0
    g21: LineSegment [constr] StartX=64.85 StartY=80.85 StartZ=0 EndX=84.85 EndY=80.85 EndZ=0
  constraints (61):
    c: Coincident(g0,g1)
    c: Coincident(g1,g2)
    c: Coincident(g2,g3)
    c: Coincident(g3,g0)
    c: Horizontal(g0)
    c: Horizontal(g2)
    c: Vertical(g1)
    c: Coincident(g4,g5)
    c: Coincident(g5,g6)
    c: Coincident(g6,g7)
    c: Coincident(g7,g4)
    c: Horizontal(g4)
    c: Horizontal(g6)
    c: Vertical(g5)
    c: Diameter(g8) = 19
    c: DistanceX(g4,g4) = 83
    c: Coincident(g9,g10)
    c: Coincident(g10,g11)
    c: Coincident(g11,g12)
    c: Coincident(g12,g9)
    c: Horizontal(g11)
    c: Vertical(g10)
    c: Vertical(g12)
    c: DistanceX(g9,g9) = 80
    c: DistanceX(g6,g11) = 2
    c: DistanceY(g9,g4) = 18
    c: DistanceY(g6,g11) = 18
    c: DistanceY(g12,g12) = 36
    c: PointOnObject(g13,g-3)
    c: PointOnObject(g13,g-6)
    c: Symmetric(g-4,g-1,g13)
    c: Symmetric(g4,g6,g13)
    c: PointOnObject(g8,g13)
    c: Symmetric(g0,g2,g13)
    c: PointOnObject(g14,g9)
    c: PointOnObject(g14,g11)
    c: Symmetric(g9,g9,g14)
    c: Symmetric(g0,g0,g14)
    c: Distance(g0) = 74
    c: Distance(g3) = 28
    c: Distance(g8,g5) = 20
    c: PointOnObject(g15,g13)
    c: PointOnObject(g13,g15)
    c: Tangent(g15,g7)
    c: PointOnObject(g16,g13)
    c: PointOnObject(g13,g16)
    c: Tangent(g16,g8)
    c: Equal(g16,g15)
    c: Tangent(g17,g20)
    c: Tangent(g17,g19)
    c: Tangent(g19,g18)
    c: Tangent(g20,g18)
    c: Horizontal(g19)
    c: Equal(g17,g18)
    c: DistanceY(g9,g18) = 9.6
    c: DistanceY(g18,g18) = 6.5
    c: PointOnObject(g21,g17)
    c: PointOnObject(g21,g18)
    c: Symmetric(g17,g17,g21)
    c: Distance(g21,g21) = 20
    c: DistanceX(g21,g9) = 15.9
FEATURE [PartDesign::Pocket] Pocket004
  BaseFeature = -> Pad002
  Length = 5
  Length2 = 100
  Placement = pos=(0,-45,1e-16) rot=(1,0,0;1.5708rad)
  Profile = -> Sketch009
  Type = 2
FEATURE [Sketcher::SketchObject] Sketch012
  MapMode = 5
  Placement = pos=(97.75,-45,0) rot=(0.707107,0,-0.707107;3.14159rad)
  sketch-geometry (5):
    g0: LineSegment StartX=-41 StartY=-1.54e-14 StartZ=0 EndX=-59 EndY=-1.54e-14 EndZ=0
    g1: LineSegment StartX=-59 StartY=-1.54e-14 StartZ=0 EndX=-59 EndY=1 EndZ=0
    g2: LineSegment StartX=-59 StartY=1 StartZ=0 EndX=-41 EndY=1 EndZ=0
    g3: LineSegment StartX=-41 StartY=1 StartZ=0 EndX=-41 EndY=-1.54e-14 EndZ=0
    g4: LineSegment [constr] StartX=-50 StartY=2 StartZ=0 EndX=-50 EndY=-1.55e-14 EndZ=0
  constraints (11):
    c: Coincident(g0,g1)
    c: Coincident(g1,g2)
    c: Coincident(g2,g3)
    c: Coincident(g3,g0)
    c: Horizontal(g0)
    c: Vertical(g1)
    c: Vertical(g3)
    c: Symmetric(g1,g2,g4)
    c: DistanceY(g1,g1) = 1
    c: DistanceX(g2,g2) = 18
    c: PointOnObject(g4,g0)
FEATURE [PartDesign::Pocket] Pocket007
  BaseFeature = -> Pocket004
  Length = 6
  Length2 = 100
  Placement = pos=(0,-45,1e-16) rot=(1,0,0;1.5708rad)
  Profile = -> Sketch012
  Type = 0
FEATURE [PartDesign::CoordinateSystem] LCS_button
  AttacherType = Attacher::AttachEngine3D
  MapMode = 11
  Placement = pos=(121.75,-47,50) rot=(0.57735,-0.57735,0.57735;2.0944rad)
  Support = -> [Pocket007]
FEATURE [Sketcher::SketchObject] Sketch
  ExternalGeometry = -> [Pocket007]
  MapMode = 5
  Placement = pos=(0,-45,1e-16) rot=(-1,0,0;1.5708rad)
  Support = -> [Pocket007]
  sketch-geometry (9):
    g0: LineSegment StartX=2 StartY=-50 StartZ=0 EndX=8 EndY=-50 EndZ=0
    g1: LineSegment StartX=8 StartY=-50 StartZ=0 EndX=8 EndY=-62 EndZ=0
    g2: LineSegment StartX=8 StartY=-62 StartZ=0 EndX=2 EndY=-62 EndZ=0
    g3: LineSegment StartX=2 StartY=-62 StartZ=0 EndX=2 EndY=-50 EndZ=0
    g4: LineSegment [constr] StartX=0 StartY=-50 StartZ=0 EndX=150 EndY=-50 EndZ=0
    g5: LineSegment StartX=142 StartY=-50 StartZ=0 EndX=148 EndY=-50 EndZ=0
    g6: LineSegment StartX=148 StartY=-50 StartZ=0 EndX=148 EndY=-62 EndZ=0
    g7: LineSegment StartX=148 StartY=-62 StartZ=0 EndX=142 EndY=-62 EndZ=0
    g8: LineSegment StartX=142 StartY=-62 StartZ=0 EndX=142 EndY=-50 EndZ=0
  constraints (27):
    c: Coincident(g0,g1)
    c: Coincident(g1,g2)
    c: Coincident(g2,g3)
    c: Coincident(g3,g0)
    c: Horizontal(g0)
    c: Horizontal(g2)
    c: Vertical(g3)
    c: PointOnObject(g4,g-4)
    c: PointOnObject(g4,g-3)
    c: Symmetric(g-1,g-5,g4)
    c: DistanceX(g4,g0) = 2
    c: DistanceY(g1,g1) = 12
    c: DistanceX(g0,g0) = 6
    c: Coincident(g5,g6)
    c: Coincident(g6,g7)
    c: Coincident(g7,g8)
    c: Coincident(g8,g5)
    c: Horizontal(g5)
    c: Horizontal(g7)
    c: Vertical(g8)
    c: Equal(g8,g1)
    c: Equal(g0,g5)
    c: DistanceX(g6,g4) = 2
    c: Vertical(g6)
    c: Vertical(g1)
    c: PointOnObject(g5,g4)
    c: PointOnObject(g0,g4)
FEATURE [PartDesign::Pad] Pad
  BaseFeature = -> Pocket007
  Direction = (1,1,1)
  Length = 8
  Length2 = 100
  Placement = pos=(0,-45,1e-16) rot=(1,0,0;1.5708rad)
  Profile = -> Sketch
  Type = 0
FEATURE [Sketcher::SketchObject] Sketch013
  ExternalGeometry = -> [Pad]
  MapMode = 5
  Placement = pos=(0,-45,50) rot=(1,0,0;3.14159rad)
  Support = -> [Pad]
  sketch-geometry (24):
    g0: LineSegment StartX=2 StartY=-8 StartZ=0 EndX=3 EndY=-8 EndZ=0
    g1: LineSegment StartX=3 StartY=-8 StartZ=0 EndX=3 EndY=-3 EndZ=0
    g2: LineSegment StartX=3 StartY=-3 StartZ=0 EndX=4 EndY=-3 EndZ=0
    g3: LineSegment StartX=4 StartY=-3 StartZ=0 EndX=4 EndY=0 EndZ=0
    g4: LineSegment StartX=4 StartY=0 StartZ=0 EndX=2 EndY=0 EndZ=0
    g5: LineSegment StartX=2 StartY=0 StartZ=0 EndX=2 EndY=-8 EndZ=0
    g6: LineSegment StartX=7 StartY=-8 StartZ=0 EndX=8 EndY=-8 EndZ=0
    g7: LineSegment StartX=8 StartY=-8 StartZ=0 EndX=8 EndY=0 EndZ=0
    g8: LineSegment StartX=8 StartY=0 StartZ=0 EndX=6 EndY=0 EndZ=0
    g9: LineSegment StartX=6 StartY=0 StartZ=0 EndX=6 EndY=-3 EndZ=0
    g10: LineSegment StartX=6 StartY=-3 StartZ=0 EndX=7 EndY=-3 EndZ=0
    g11: LineSegment StartX=7 StartY=-3 StartZ=0 EndX=7 EndY=-8 EndZ=0
    g12: LineSegment StartX=142 StartY=-8 StartZ=0 EndX=143 EndY=-8 EndZ=0
    g13: LineSegment StartX=143 StartY=-8 StartZ=0 EndX=143 EndY=-3 EndZ=0
    g14: LineSegment StartX=143 StartY=-3 StartZ=0 EndX=144 EndY=-3 EndZ=0
    g15: LineSegment StartX=144 StartY=-3 StartZ=0 EndX=144 EndY=1.2e-14 EndZ=0
    g16: LineSegment StartX=144 StartY=1.2e-14 StartZ=0 EndX=142 EndY=0 EndZ=0
    g17: LineSegment StartX=142 StartY=0 StartZ=0 EndX=142 EndY=-8 EndZ=0
    g18: LineSegment StartX=146 StartY=0 StartZ=0 EndX=146 EndY=-3 EndZ=0
    g19: LineSegment StartX=146 StartY=-3 StartZ=0 EndX=147 EndY=-3 EndZ=0
    g20: LineSegment StartX=147 StartY=-3 StartZ=0 EndX=147 EndY=-8 EndZ=0
    g21: LineSegment StartX=147 StartY=-8 StartZ=0 EndX=148 EndY=-8 EndZ=0
    g22: LineSegment StartX=148 StartY=-8 StartZ=0 EndX=148 EndY=0 EndZ=0
    g23: LineSegment StartX=148 StartY=0 StartZ=0 EndX=146 EndY=0 EndZ=0
  constraints (64):
    c: Coincident(g-5,g0)
    c: PointOnObject(g0,g-3)
    c: Coincident(g0,g1)
    c: Vertical(g1)
    c: Coincident(g1,g2)
    c: Horizontal(g2)
    c: Coincident(g2,g3)
    c: PointOnObject(g3,g-6)
    c: Vertical(g3)
    c: Coincident(g3,g4)
    c: Coincident(g4,g-5)
    c: Coincident(g4,g5)
    c: Coincident(g5,g0)
    c: DistanceX(g0,g0) = 1
    c: DistanceY(g1,g1) = 5
    c: DistanceX(g2,g2) = 1
    c: PointOnObject(g6,g-3)
    c: Coincident(g6,g-4)
    c: Coincident(g6,g7)
    c: Coincident(g7,g-4)
    c: Coincident(g7,g8)
    c: PointOnObject(g8,g-6)
    c: Coincident(g8,g9)
    c: Vertical(g9)
    c: Coincident(g9,g10)
    c: Coincident(g10,g11)
    c: Coincident(g11,g6)
    c: Vertical(g11)
    c: Equal(g2,g10)
    c: Equal(g9,g3)
    c: Equal(g11,g1)
    c: Equal(g6,g0)
    c: Coincident(g-9,g12)
    c: PointOnObject(g12,g-9)
    c: Coincident(g12,g13)
    c: Vertical(g13)
    c: Coincident(g13,g14)
    c: Horizontal(g14)
    c: Coincident(g14,g15)
    c: Vertical(g15)
    c: Coincident(g15,g16)
    c: Coincident(g16,g-7)
    c: Coincident(g16,g17)
    c: Coincident(g17,g12)
    c: PointOnObject(g18,g-6)
    c: Vertical(g18)
    c: Coincident(g18,g19)
    c: Horizontal(g19)
    c: Coincident(g19,g20)
    c: Vertical(g20)
    c: Coincident(g20,g21)
    c: Coincident(g21,g-9)
    c: Coincident(g21,g22)
    c: Coincident(g22,g-8)
    c: Coincident(g22,g23)
    c: Coincident(g23,g18)
    c: Equal(g12,g21)
    c: Equal(g13,g20)
    c: Equal(g14,g19)
    c: Equal(g15,g18)
    c: Equal(g12,g6)
    c: Equal(g11,g20)
    c: Equal(g15,g9)
    c: Equal(g2,g14)
FEATURE [PartDesign::Pocket] Pocket
  Length = 12
  Length2 = 6
  Placement = pos=(0,-45,1e-16) rot=(1,0,0;1.5708rad)
  Profile = -> Sketch013
  Type = 0
FEATURE [Sketcher::SketchObject] Sketch014
  ExternalGeometry = -> [Pocket]
  MapMode = 5
  Placement = pos=(0,-45,1e-16) rot=(-1,0,0;1.5708rad)
  Support = -> [Pocket]
  sketch-geometry (9):
    g0: LineSegment [constr] StartX=18.75 StartY=-14 StartZ=0 EndX=101.75 EndY=-14 EndZ=0
    g1: LineSegment [constr] StartX=101.75 StartY=-14 StartZ=0 EndX=101.75 EndY=-86 EndZ=0
    g2: LineSegment [constr] StartX=101.75 StartY=-86 StartZ=0 EndX=18.75 EndY=-86 EndZ=0
    g3: LineSegment [constr] StartX=18.75 StartY=-86 StartZ=0 EndX=18.75 EndY=-14 EndZ=0
    g4: LineSegment [constr] StartX=150 StartY=-50 StartZ=0 EndX=0 EndY=-50 EndZ=0
    g5: Circle CenterX=95.75 CenterY=-80 CenterZ=0 NormalX=0 NormalY=0 NormalZ=1 AngleXU=0 Radius=3
    g6: Circle CenterX=24.75 CenterY=-80 CenterZ=0 NormalX=0 NormalY=0 NormalZ=1 AngleXU=0 Radius=3
    g7: Circle CenterX=95.75 CenterY=-20 CenterZ=0 NormalX=0 NormalY=0 NormalZ=1 AngleXU=0 Radius=3
    g8: Circle CenterX=24.75 CenterY=-20 CenterZ=0 NormalX=0 NormalY=0 NormalZ=1 AngleXU=0 Radius=3
  constraints (26):
    c: Coincident(g0,g1)
    c: Coincident(g1,g2)
    c: Coincident(g2,g3)
    c: Coincident(g3,g0)
    c: Horizontal(g0)
    c: Horizontal(g2)
    c: Vertical(g1)
    c: DistanceX(g2,g2) = 83
    c: DistanceY(g3,g3) = 72
    c: PointOnObject(g4,g-5)
    c: Symmetric(g-5,g-1,g4)
    c: Symmetric(g2,g0,g4)
    c: Distance(g-8,g1) = 20
    c: Diameter(g5) = 6
    c: DistanceX(g5,g1) = 6
    c: DistanceY(g1,g5) = 6
    c: Equal(g5,g6)
    c: Equal(g7,g6)
    c: Equal(g7,g8)
    c: Horizontal(g6,g5)
    c: Vertical(g5,g7)
    c: DistanceY(g7,g0) = 6
    c: Horizontal(g8,g7)
    c: Vertical(g6,g8)
    c: DistanceX(g2,g6) = 6
    c: PointOnObject(g4,g-4)
FEATURE [PartDesign::Pad] Pad003
  BaseFeature = -> Pocket
  Direction = (1,1,1)
  Length = 18
  Length2 = 100
  Placement = pos=(0,-45,1e-16) rot=(1,0,0;1.5708rad)
  Profile = -> Sketch014
  Type = 0
FEATURE [Sketcher::SketchObject] Sketch015
  ExternalGeometry = -> [Pad003]
  MapMode = 5
  Placement = pos=(-1.42e-14,-27,-6.6e-15) rot=(-1,0,0;1.5708rad)
  Support = -> [Pad003]
  sketch-geometry (19):
    g0: Circle [constr] CenterX=95.75 CenterY=-80 CenterZ=0 NormalX=0 NormalY=0 NormalZ=1 AngleXU=0 Radius=1.5
    g1: LineSegment [constr] StartX=97.25 StartY=-80 StartZ=0 EndX=97.25 EndY=-77.4019 EndZ=0
    g2: LineSegment [constr] StartX=94.25 StartY=-80 StartZ=0 EndX=94.25 EndY=-77.4019 EndZ=0
    g3: ArcOfCircle CenterX=95.75 CenterY=-80 CenterZ=0 NormalX=0 NormalY=0 NormalZ=1 AngleXU=0 Radius=1.5 StartAngle=3.14159 EndAngle=6.28319
    g4: LineSegment StartX=97.25 StartY=-80 StartZ=0 EndX=97.25 EndY=-77.4019 EndZ=0
    g5: LineSegment StartX=94.25 StartY=-80 StartZ=0 EndX=94.25 EndY=-77.4019 EndZ=0
    g6: ArcOfCircle CenterX=95.75 CenterY=-80 CenterZ=0 NormalX=0 NormalY=0 NormalZ=1 AngleXU=0 Radius=3 StartAngle=1.0472 EndAngle=2.0944
    g7: ArcOfCircle CenterX=24.75 CenterY=-80 CenterZ=0 NormalX=0 NormalY=0 NormalZ=1 AngleXU=0 Radius=1.5 StartAngle=3.14159 EndAngle=6.28319
    g8: ArcOfCircle CenterX=24.75 CenterY=-80 CenterZ=0 NormalX=0 NormalY=0 NormalZ=1 AngleXU=0 Radius=3 StartAngle=1.0472 EndAngle=2.0944
    g9: LineSegment StartX=26.25 StartY=-80 StartZ=0 EndX=26.25 EndY=-77.4019 EndZ=0
    g10: LineSegment StartX=23.25 StartY=-80 StartZ=0 EndX=23.25 EndY=-77.4019 EndZ=0
    g11: ArcOfCircle CenterX=95.75 CenterY=-20 CenterZ=0 NormalX=0 NormalY=0 NormalZ=1 AngleXU=0 Radius=1.5 StartAngle=3.14159 EndAngle=6.28319
    g12: ArcOfCircle CenterX=95.75 CenterY=-20 CenterZ=0 NormalX=0 NormalY=0 NormalZ=1 AngleXU=0 Radius=3 StartAngle=1.0472 EndAngle=2.0944
    g13: LineSegment StartX=97.25 StartY=-20 StartZ=0 EndX=97.25 EndY=-17.4019 EndZ=0
    g14: LineSegment StartX=94.25 StartY=-20 StartZ=0 EndX=94.25 EndY=-17.4019 EndZ=0
    g15: ArcOfCircle CenterX=24.75 CenterY=-20 CenterZ=0 NormalX=0 NormalY=0 NormalZ=1 AngleXU=0 Radius=1.5 StartAngle=3.14159 EndAngle=6.28319
    g16: ArcOfCircle CenterX=24.75 CenterY=-20 CenterZ=0 NormalX=0 NormalY=0 NormalZ=1 AngleXU=0 Radius=3 StartAngle=1.0472 EndAngle=2.0944
    g17: LineSegment StartX=26.25 StartY=-20 StartZ=0 EndX=26.25 EndY=-17.4019 EndZ=0
    g18: LineSegment StartX=23.25 StartY=-20 StartZ=0 EndX=23.25 EndY=-17.4019 EndZ=0
  constraints (54):
    c: Diameter(g0) = 3
    c: PointOnObject(g1,g0)
    c: PointOnObject(g1,g-3)
    c: PointOnObject(g2,g-3)
    c: Vertical(g2)
    c: Vertical(g1)
    c: Coincident(g3,g0)
    c: Coincident(g3,g1)
    c: Coincident(g3,g2)
    c: Coincident(g4,g3)
    c: Coincident(g4,g1)
    c: Coincident(g5,g3)
    c: Coincident(g5,g2)
    c: Coincident(g6,g3)
    c: Coincident(g6,g4)
    c: Coincident(g6,g5)
    c: Coincident(g7,g-4)
    c: Coincident(g8,g7)
    c: PointOnObject(g8,g-4)
    c: Coincident(g9,g8)
    c: Vertical(g9)
    c: Coincident(g10,g7)
    c: Coincident(g10,g8)
    c: Vertical(g10)
    c: Tangent(g9,g7) = -1.5708
    c: Equal(g8,g6)
    c: Equal(g7,g3)
    c: Equal(g9,g5)
    c: Equal(g9,g10)
    c: Equal(g4,g5)
    c: Coincident(g11,g-5)
    c: Coincident(g12,g11)
    c: PointOnObject(g12,g-5)
    c: Coincident(g13,g11)
    c: Coincident(g13,g12)
    c: Coincident(g14,g11)
    c: Coincident(g14,g12)
    c: Vertical(g14)
    c: Equal(g13,g14)
    c: Equal(g14,g10)
    c: Equal(g7,g11)
    c: Vertical(g13)
    c: Coincident(g15,g-6)
    c: Coincident(g16,g15)
    c: PointOnObject(g16,g-6)
    c: Coincident(g17,g15)
    c: Coincident(g17,g16)
    c: Coincident(g18,g15)
    c: Coincident(g18,g16)
    c: Vertical(g17)
    c: Vertical(g18)
    c: Equal(g17,g18)
    c: Equal(g15,g7)
    c: Equal(g18,g10)
FEATURE [PartDesign::Pocket] Pocket008
  BaseFeature = -> Pad003
  Length = 10
  Length2 = 100
  Placement = pos=(0,-45,1e-16) rot=(1,0,0;1.5708rad)
  Profile = -> Sketch015
  Type = 0
FEATURE [PartDesign::Body] Body
  Group = -> [Pocket,Sketch014,Pad003,Sketch015,Pocket008]
  Origin = -> Origin
  Tip = -> Pocket008
FEATURE [PartDesign::Pocket] Pocket009
  BaseFeature = -> Pad
  Length = 12
  Length2 = 100
  Placement = pos=(0,-45,1e-16) rot=(1,0,0;1.5708rad)
  Profile = -> Sketch013
  Type = 0
FEATURE [PartDesign::Body] Body001  label="coperchio"
  Group = -> [Sketch008,Pad002,Sketch009,Pocket004,Sketch012,Pocket007,Sketch,Pad,Sketch013,Pocket009]
  Origin = -> Origin001
  Tip = -> Pocket009
FEATURE [Part::MultiFuse] Fusion
  Shapes = -> [Body001,Extrude002,Body]
FEATURE [PartDesign::CoordinateSystem] LCS_box
  AttacherType = Attacher::AttachEngine3D
  MapMode = 7
  Placement = pos=(3,-37,50) rot=(0.57735,-0.57735,-0.57735;2.0944rad)
  Support = -> [Fusion]
FEATURE [Part::Fillet] Fillet
  Base = -> Fusion
  Edges = 4 edges r=2: [Edge1,Edge2,Edge5,Edge8]
FEATURE [Part::Fillet] Fillet001
  Base = -> Fillet
  Edges = 4 edges r=1: [Edge54,Edge55,Edge56,Edge57]
FEATURE [App::Part] Part  label="coperchio_completo"
  Group = -> [Body001,ShapeString,Extrude002,LCS_box,LCS_button,Body,Fusion,Fillet,Fillet001]
  Origin = -> Origin002
note: 1 file-system path scrubbed to <path> (originals preserved in the JSON sidecar)
---- part lcd.FCStd = doc fcstd_a03994c6dc0d ----
FCSTD DOCUMENT  (FreeCAD 0.19R22665 (Git))
Label: lcd
License: All rights reserved
LicenseURL: http://en.wikipedia.org/wiki/All_rights_reserved
objects: Sketcher::SketchObject×7, PartDesign::Pad×4, PartDesign::Pocket×3, PartDesign::Body×2, PartDesign::ShapeBinder×1, Part::FeaturePython×1, PartDesign::CoordinateSystem×1, App::Part×1
note: 26 computed .brp shape members not serialized (recipe doc carries the construction recipe); baked Part::Feature solids carry a one-line shape summary decoded from their .brp

FEATURE [Sketcher::SketchObject] Sketch003
  MapMode = 5
  Support = -> [XY_Plane001]
  sketch-geometry (4):
    g0: LineSegment StartX=-80 StartY=36 StartZ=0 EndX=0 EndY=36 EndZ=0
    g1: LineSegment StartX=0 StartY=36 StartZ=0 EndX=0 EndY=0 EndZ=0
    g2: LineSegment StartX=0 StartY=0 StartZ=0 EndX=-80 EndY=0 EndZ=0
    g3: LineSegment StartX=-80 StartY=0 StartZ=0 EndX=-80 EndY=36 EndZ=0
  constraints (11):
    c: Coincident(g0,g1)
    c: Coincident(g1,g2)
    c: Coincident(g2,g3)
    c: Coincident(g3,g0)
    c: Horizontal(g0)
    c: Horizontal(g2)
    c: Vertical(g1)
    c: Vertical(g3)
    c: Coincident(g1,g-1)
    c: Distance(g1) = 36
    c: Distance(g2) = 80
FEATURE [PartDesign::Pad] Pad001  label="Pad002"
  AllowMultiFace = false
  Direction = (1,1,1)
  Length = 1.6
  Length2 = 100
  Profile = -> Sketch003
  Type = 0
FEATURE [Sketcher::SketchObject] Sketch004
  ExternalGeometry = -> [Pad001]
  MapMode = 5
  Placement = pos=(0,0,1.6) rot=(0,0,1;0rad)
  Support = -> [Pad001]
  sketch-geometry (4):
    g0: Circle CenterX=-77.7 CenterY=33.5 CenterZ=0 NormalX=0 NormalY=0 NormalZ=1 AngleXU=0 Radius=1.4
    g1: Circle CenterX=-77.7 CenterY=2.1 CenterZ=0 NormalX=0 NormalY=0 NormalZ=1 AngleXU=0 Radius=1.4
    g2: Circle CenterX=-2.3 CenterY=33.5 CenterZ=0 NormalX=0 NormalY=0 NormalZ=1 AngleXU=0 Radius=1.4
    g3: Circle CenterX=-2.3 CenterY=2.1 CenterZ=0 NormalX=0 NormalY=0 NormalZ=1 AngleXU=0 Radius=1.4
  constraints (12):
    c: Horizontal(g0,g2)
    c: Horizontal(g1,g3)
    c: Vertical(g0,g1)
    c: Vertical(g2,g3)
    c: Equal(g0,g1)
    c: Equal(g1,g2)
    c: Equal(g2,g3)
    c: Radius(g0) = 1.4
    c: Distance(g0,g1) = 31.4
    c: Distance(g0,g2) = 75.4
    c: DistanceY(g2,g-3) = 2.5
    c: DistanceX(g2,g-3) = 2.3
FEATURE [PartDesign::Pocket] Pocket001
  AllowMultiFace = false
  BaseFeature = -> Pad001
  Length = 5
  Length2 = 100
  Profile = -> Sketch004
  Type = 1
FEATURE [Sketcher::SketchObject] Sketch005
  ExternalGeometry = -> [Pocket001]
  MapMode = 5
  Placement = pos=(0,0,1.6) rot=(0,0,1;0rad)
  Support = -> [Pocket001]
  sketch-geometry (16):
    g0: Circle CenterX=-72 CenterY=33.5 CenterZ=0 NormalX=0 NormalY=0 NormalZ=1 AngleXU=0 Radius=0.5
    g1: Circle CenterX=-69.46 CenterY=33.5 CenterZ=0 NormalX=0 NormalY=0 NormalZ=1 AngleXU=0 Radius=0.5
    g2: Circle CenterX=-64.38 CenterY=33.5 CenterZ=0 NormalX=0 NormalY=0 NormalZ=1 AngleXU=0 Radius=0.5
    g3: Circle CenterX=-59.3 CenterY=33.5 CenterZ=0 NormalX=0 NormalY=0 NormalZ=1 AngleXU=0 Radius=0.5
    g4: Circle CenterX=-66.92 CenterY=33.5 CenterZ=0 NormalX=0 NormalY=0 NormalZ=1 AngleXU=0 Radius=0.5
    g5: Circle CenterX=-61.84 CenterY=33.5 CenterZ=0 NormalX=0 NormalY=0 NormalZ=1 AngleXU=0 Radius=0.5
    g6: Circle CenterX=-56.76 CenterY=33.5 CenterZ=0 NormalX=0 NormalY=0 NormalZ=1 AngleXU=0 Radius=0.5
    g7: Circle CenterX=-51.68 CenterY=33.5 CenterZ=0 NormalX=0 NormalY=0 NormalZ=1 AngleXU=0 Radius=0.5
    g8: Circle CenterX=-54.22 CenterY=33.5 CenterZ=0 NormalX=0 NormalY=0 NormalZ=1 AngleXU=0 Radius=0.5
    g9: Circle CenterX=-49.14 CenterY=33.5 CenterZ=0 NormalX=0 NormalY=0 NormalZ=1 AngleXU=0 Radius=0.5
    g10: Circle CenterX=-46.6 CenterY=33.5 CenterZ=0 NormalX=0 NormalY=0 NormalZ=1 AngleXU=0 Radius=0.5
    g11: Circle CenterX=-36.44 CenterY=33.5 CenterZ=0 NormalX=0 NormalY=0 NormalZ=1 AngleXU=0 Radius=0.5
    g12: Circle CenterX=-44.06 CenterY=33.5 CenterZ=0 NormalX=0 NormalY=0 NormalZ=1 AngleXU=0 Radius=0.5
    g13: Circle CenterX=-38.98 CenterY=33.5 CenterZ=0 NormalX=0 NormalY=0 NormalZ=1 AngleXU=0 Radius=0.5
    g14: Circle CenterX=-33.9 CenterY=33.5 CenterZ=0 NormalX=0 NormalY=0 NormalZ=1 AngleXU=0 Radius=0.5
    g15: Circle CenterX=-41.52 CenterY=33.5 CenterZ=0 NormalX=0 NormalY=0 NormalZ=1 AngleXU=0 Radius=0.5
  constraints (48):
    c: Radius(g0) = 0.5
    c: DistanceX(g-3,g0) = 8
    c: DistanceY(g0,g-3) = 2.5
    c: Equal(g0,g1) = 0.5
    c: Equal(g1,g2)
    c: Equal(g2,g3)
    c: Equal(g0,g4) = 0.5
    c: Equal(g4,g5) = 0.5
    c: Equal(g5,g6)
    c: Equal(g6,g7)
    c: Equal(g0,g8) = 0.5
    c: Equal(g8,g9) = 0.5
    c: Equal(g9,g10)
    c: Equal(g10,g11)
    c: Equal(g8,g12) = 0.5
    c: Equal(g12,g13) = 0.5
    c: Equal(g13,g14)
    c: Equal(g14,g15)
    c: Horizontal(g0,g1)
    c: Horizontal(g1,g4)
    c: Horizontal(g4,g2)
    c: Horizontal(g5,g3)
    c: Horizontal(g3,g6)
    c: Horizontal(g6,g8)
    c: Horizontal(g7,g9)
    c: Horizontal(g9,g10)
    c: Horizontal(g10,g12)
    c: Horizontal(g15,g13)
    c: Horizontal(g13,g11)
    c: Horizontal(g11,g14)
    c: Horizontal(g2,g5)
    c: Horizontal(g5,g7)
    c: Horizontal(g12,g15)
    c: Distance(g0,g1) = 2.54
    c: Distance(g1,g4) = 2.54
    c: Distance(g4,g2) = 2.54
    c: Distance(g2,g5) = 2.54
    c: Distance(g5,g3) = 2.54
    c: Distance(g6,g3) = 2.54
    c: Distance(g8,g6) = 2.54
    c: Distance(g8,g7) = 2.54
    c: Distance(g7,g9) = 2.54
    c: Distance(g9,g10) = 2.54
    c: Distance(g10,g12) = 2.54
    c: Distance(g15,g12) = 2.54
    c: Distance(g15,g13) = 2.54
    c: Distance(g13,g11) = 2.54
    c: Distance(g11,g14) = 2.54
FEATURE [PartDesign::Pocket] Pocket002
  AllowMultiFace = false
  BaseFeature = -> Pocket001
  Length = 5
  Length2 = 100
  Profile = -> Sketch005
  Type = 1
FEATURE [PartDesign::ShapeBinder] ShapeBinder
  Support = -> [Pocket002]
  TraceSupport = false
FEATURE [Sketcher::SketchObject] Sketch
  ExternalGeometry = -> [ShapeBinder]
  MapMode = 5
  Support = -> [XY_Plane]
  sketch-geometry (6):
    g0: LineSegment StartX=-75.35 StartY=29.9 StartZ=0 EndX=-4.65 EndY=29.9 EndZ=0
    g1: LineSegment StartX=-4.65 StartY=29.9 StartZ=0 EndX=-4.65 EndY=6.1 EndZ=0
    g2: LineSegment StartX=-4.65 StartY=6.1 StartZ=0 EndX=-75.35 EndY=6.1 EndZ=0
    g3: LineSegment StartX=-75.35 StartY=6.1 StartZ=0 EndX=-75.35 EndY=29.9 EndZ=0
    g4: LineSegment [constr] StartX=-75.35 StartY=18 StartZ=0 EndX=-4.65 EndY=18 EndZ=0
    g5: LineSegment [constr] StartX=-40 StartY=29.9 StartZ=0 EndX=-40 EndY=6.1 EndZ=0
  constraints (16):
    c: Coincident(g0,g1)
    c: Coincident(g1,g2)
    c: Coincident(g2,g3)
    c: Coincident(g3,g0)
    c: Horizontal(g2)
    c: Vertical(g1)
    c: Distance(g0) = 70.7
    c: Distance(g3) = 23.8
    c: Symmetric(g0,g2,g4)
    c: PointOnObject(g4,g3)
    c: PointOnObject(g4,g1)
    c: Symmetric(g-3,g-4,g4)
    c: PointOnObject(g5,g0)
    c: PointOnObject(g5,g2)
    c: Symmetric(g0,g0,g5)
    c: Symmetric(g-3,g-3,g5)
FEATURE [PartDesign::Pad] Pad
  AllowMultiFace = false
  Direction = (1,1,1)
  Length = 11
  Length2 = 100
  Profile = -> Sketch
  Type = 0
FEATURE [Sketcher::SketchObject] Sketch001
  ExternalGeometry = -> [Pad]
  MapMode = 5
  Placement = pos=(0,0,0) rot=(1,0,0;3.14159rad)
  Support = -> [Pad]
  sketch-geometry (4):
    g0: LineSegment StartX=-75.35 StartY=-7.1 StartZ=0 EndX=-4.65 EndY=-7.1 EndZ=0
    g1: LineSegment StartX=-4.65 StartY=-7.1 StartZ=0 EndX=-4.65 EndY=-28.9 EndZ=0
    g2: LineSegment StartX=-4.65 StartY=-28.9 StartZ=0 EndX=-75.35 EndY=-28.9 EndZ=0
    g3: LineSegment StartX=-75.35 StartY=-28.9 StartZ=0 EndX=-75.35 EndY=-7.1 EndZ=0
  constraints (12):
    c: Coincident(g0,g1)
    c: Coincident(g1,g2)
    c: Coincident(g2,g3)
    c: Coincident(g3,g0)
    c: Horizontal(g0)
    c: Horizontal(g2)
    c: Vertical(g1)
    c: Vertical(g3)
    c: DistanceY(g0,g-3) = 1
    c: DistanceY(g-3,g2) = 1
    c: DistanceX(g-3,g0) = 0
    c: DistanceX(g0,g-4) = 0
FEATURE [PartDesign::Pocket] Pocket
  AllowMultiFace = false
  BaseFeature = -> Pad
  Length = 8.6
  Length2 = 100
  Profile = -> Sketch001
  Type = 0
FEATURE [Sketcher::SketchObject] Sketch002
  ExternalGeometry = -> [Pocket]
  MapMode = 5
  Placement = pos=(0,0,11) rot=(0,0,1;0rad)
  Support = -> [Pocket]
  sketch-geometry (4):
    g0: LineSegment StartX=-74.8 StartY=25.25 StartZ=0 EndX=-5.2 EndY=25.25 EndZ=0
    g1: LineSegment StartX=-5.2 StartY=25.25 StartZ=0 EndX=-5.2 EndY=10.75 EndZ=0
    g2: LineSegment StartX=-5.2 StartY=10.75 StartZ=0 EndX=-74.8 EndY=10.75 EndZ=0
    g3: LineSegment StartX=-74.8 StartY=10.75 StartZ=0 EndX=-74.8 EndY=25.25 EndZ=0
  constraints (12):
    c: Coincident(g0,g1)
    c: Coincident(g1,g2)
    c: Coincident(g2,g3)
    c: Coincident(g3,g0)
    c: Horizontal(g0)
    c: Horizontal(g2)
    c: Vertical(g1)
    c: Vertical(g3)
    c: Distance(g0) = 69.6
    c: Distance(g3) = 14.5
    c: DistanceX(g-3,g0) = 0.55
    c: DistanceY(g0,g-3) = 4.65
FEATURE [PartDesign::Pad] Pad002  label="Pad003"
  AllowMultiFace = false
  BaseFeature = -> Pocket
  Direction = (1,1,1)
  Length = 0.1
  Length2 = 100
  Profile = -> Sketch002
  Type = 0
FEATURE [PartDesign::Body] Body  label="corpo_lcd"
  Group = -> [Sketch,Pad,Sketch001,Pocket,Sketch002,ShapeBinder,Pad002]
  Origin = -> Origin
  Placement = pos=(0,0,-2.4) rot=(0,0,1;0rad)
  Tip = -> Pad002
FEATURE [Sketcher::SketchObject] Sketch006
  ExternalGeometry = -> [Pocket002]
  MapMode = 5
  Placement = pos=(0,0,0) rot=(1,0,0;3.14159rad)
  Support = -> [Pocket002]
  sketch-geometry (5):
    g0: LineSegment StartX=-73.25 StartY=-32.25 StartZ=0 EndX=-32.65 EndY=-32.25 EndZ=0
    g1: LineSegment StartX=-32.65 StartY=-32.25 StartZ=0 EndX=-32.65 EndY=-34.75 EndZ=0
    g2: LineSegment StartX=-32.65 StartY=-34.75 StartZ=0 EndX=-73.25 EndY=-34.75 EndZ=0
    g3: LineSegment StartX=-73.25 StartY=-34.75 StartZ=0 EndX=-73.25 EndY=-32.25 EndZ=0
    g4: LineSegment [constr] StartX=-73.25 StartY=-33.5 StartZ=0 EndX=-69.46 EndY=-33.5 EndZ=0
  constraints (14):
    c: Coincident(g0,g1)
    c: Coincident(g1,g2)
    c: Coincident(g2,g3)
    c: Coincident(g3,g0)
    c: Horizontal(g0)
    c: Horizontal(g2)
    c: Vertical(g1)
    c: Vertical(g3)
    c: Distance(g3) = 2.5
    c: Coincident(g-5,g4)
    c: PointOnObject(g4,g3)
    c: Symmetric(g0,g2,g4)
    c: DistanceX(g2,g-4) = 1.25
    c: DistanceX(g-6,g1) = 1.25
FEATURE [PartDesign::Pad] Pad003  label="Pad004"
  AllowMultiFace = false
  BaseFeature = -> Pocket002
  Direction = (1,1,1)
  Length = 2.5
  Length2 = 100
  Profile = -> Sketch006
  Type = 0
FEATURE [PartDesign::Body] Body001  label="pcb"
  Group = -> [Sketch003,Pad001,Sketch004,Pocket001,Sketch005,Pocket002,Sketch006,Pad003]
  Origin = -> Origin001
  Tip = -> Pad003
FEATURE [Part::FeaturePython] BooleanFragments  # WARN: FeaturePython — macro-defined, semantics opaque (R4)
  Mode = 0
  Objects = -> [Body001,Body]
  Tolerance = 0
FEATURE [PartDesign::CoordinateSystem] LCS_pcb
  AttacherType = Attacher::AttachEngine3D
  MapMode = 7
  Placement = pos=(-73.25,34.75,-2.5) rot=(0,0.707107,0.707107;3.14159rad)
  Support = -> [Pad003]
FEATURE [App::Part] Part  label="lcd_block"
  Group = -> [Body,Body001,BooleanFragments,LCS_pcb]
  Origin = -> Origin002
---- part pcb_board.FCStd = doc fcstd_fe1f423b4031 ----
FCSTD DOCUMENT  (FreeCAD 0.19R22665 (Git))
Label: pcb_board
License: All rights reserved
LicenseURL: http://en.wikipedia.org/wiki/All_rights_reserved
objects: App::Link×20, Part::Feature×19, App::Part×6, PartDesign::CoordinateSystem×3, Sketcher::SketchObject×1
note: 23 computed .brp shape members not serialized (recipe doc carries the construction recipe); baked Part::Feature solids carry a one-line shape summary decoded from their .brp

FEATURE [PartDesign::CoordinateSystem] Local_CS_8929
  AttacherType = Attacher::AttachEngine3D
FEATURE [Part::Feature] Pcb_8929
  shape: bbox 83 x 72 x 1.6 mm, 170 faces (baked)
FEATURE [Sketcher::SketchObject] PCB_Sketch_8929
  sketch-geometry (8):
    g0: LineSegment StartX=93 StartY=-68 StartZ=0 EndX=164 EndY=-68 EndZ=0
    g1: LineSegment StartX=170 StartY=-134 StartZ=0 EndX=170 EndY=-74 EndZ=0
    g2: LineSegment StartX=93 StartY=-140 StartZ=0 EndX=164 EndY=-140 EndZ=0
    g3: LineSegment StartX=87 StartY=-74 StartZ=0 EndX=87 EndY=-134 EndZ=0
    g4: ArcOfCircle CenterX=164 CenterY=-74 CenterZ=0 NormalX=0 NormalY=0 NormalZ=1 AngleXU=0 Radius=6 StartAngle=0 EndAngle=1.5708
    g5: ArcOfCircle CenterX=93 CenterY=-134 CenterZ=0 NormalX=0 NormalY=0 NormalZ=1 AngleXU=0 Radius=6 StartAngle=3.14159 EndAngle=4.71239
    g6: ArcOfCircle CenterX=164 CenterY=-134 CenterZ=0 NormalX=0 NormalY=0 NormalZ=1 AngleXU=0 Radius=6 StartAngle=4.71239 EndAngle=6.28319
    g7: ArcOfCircle CenterX=93 CenterY=-74 CenterZ=0 NormalX=0 NormalY=0 NormalZ=1 AngleXU=0 Radius=6 StartAngle=1.5708 EndAngle=3.14159
  constraints (8):
    c: Coincident(g3,g5)
    c: Coincident(g3,g7)
    c: Coincident(g2,g5)
    c: Coincident(g0,g7)
    c: Coincident(g2,g6)
    c: Coincident(g0,g4)
    c: Coincident(g1,g6)
    c: Coincident(g1,g4)
FEATURE [App::Part] Board_Geoms_8929
  Group = -> [Local_CS_8929,Pcb_8929,PCB_Sketch_8929]
  Origin = -> Origin
FEATURE [Part::Feature] Shape  label="J6_PinSocket_1x04_P254mm_Vertical_5FCA8662"
  Placement = pos=(112.235,-95.42,-1.6) rot=(0.707107,-0.707107,0;3.14159rad)
  shape: bbox 10.16 x 2.54 x 10.1 mm, 134 faces (baked)
FEATURE [Part::Feature] Shape001  label="SW1_SW_PUSH_6mm_h5mm_5FCE63C8"
  Placement = pos=(95.29,-120.64,0) rot=(0,0,1;0rad)
  shape: bbox 7.174 x 6 x 8.5 mm, 105 faces (baked)
FEATURE [Part::Feature] Shape002  label="J7_PinSocket_1x05_P254mm_Vertical_5FC31174"
  Placement = pos=(114.78,-114.07,-1.6) rot=(0.707107,0.707107,0;3.14159rad)
  shape: bbox 12.7 x 2.54 x 10.1 mm, 165 faces (baked)
FEATURE [Part::Feature] Shape003  label="RV1_ACP470_5F3BE09B"
  Placement = pos=(104.5,-78.4,0) rot=(0,0,-1;1.5708rad)
  shape: bbox 9.8 x 10 x 9 mm, 36 faces (baked)
FEATURE [App::Link] RV1_ACP470_5F3BE09B_ln_  label="RV1_ACP470_5F3BE09B[2]"
  LinkPlacement = pos=(104.5,-78.4,0) rot=(0,0,-1;1.5708rad)
  LinkedObject = -> Shape003
  Placement = pos=(104.5,-78.4,0) rot=(0,0,-1;1.5708rad)
FEATURE [Part::Feature] Shape004  label="D4_LED_D5.0mm_5FA6C0E4"
  Placement = pos=(148.6,-73.4,0) rot=(0,0,1;0rad)
  shape: bbox 5.4 x 5.8 x 14.1 mm, 16 faces (baked)
FEATURE [Part::Feature] Shape005  label="F1_MF-MSMF050_5FB19120[2]"
  Placement = pos=(155.79,-94.15,0) rot=(0,0,1;1.5708rad)
  shape: bbox 3.41 x 4.73 x 1.1 mm, 14 faces (baked)
FEATURE [App::Link] F1_MF_MSMF050_5FB19120_2__ln_  label="F1_MF-MSMF050_5FB19120[3]"
  LinkPlacement = pos=(155.79,-94.15,0) rot=(0,0,1;1.5708rad)
  LinkedObject = -> Shape005
  Placement = pos=(155.79,-94.15,0) rot=(0,0,1;1.5708rad)
FEATURE [Part::Feature] Shape006  label="U3_SOT_23_6_5FB065DB"
  Placement = pos=(155.53,-81.77,-1.6) rot=(0,1,0;3.14159rad)
  shape: bbox 2.8 x 2.9 x 1.55 mm, 124 faces (baked)
FEATURE [Part::Feature] Shape007  label="D3_D_DO-41_SOD81_P7.62mm_Horizontal_5FCE6338"
  Placement = pos=(102.89,-128.56,0) rot=(0,0,1;3.14159rad)
  shape: bbox 8.618 x 2.72 x 5.71 mm, 15 faces (baked)
FEATURE [Part::Feature] Shape008  label="C5_C_Disc_D50mm_W25mm_P250mm_5FB07593"
  Placement = pos=(158.04,-78.42,0) rot=(0,0,1;3.14159rad)
  shape: bbox 5 x 2.5 x 7.1 mm, 6 faces (baked)
FEATURE [Part::Feature] Part__Feature  label="TB001-500-02P_Green - P"
  shape: bbox 9 x 16.9 x 10.5 mm, 145 faces (baked)
FEATURE [Part::Feature] Part__Feature001  label="TB001-500-02P_Green - P001"
  Placement = pos=(0,0,10) rot=(0,0,1;0rad)
  shape: bbox 9 x 16.9 x 10.5 mm, 145 faces (baked)
FEATURE [App::Part] CUI_DEVICES_TB001_500_P04GR  label="J2_CUI_DEVICES_TB001-500-P04GR_5FCB9D5E[2]"
  Group = -> [Part__Feature,Part__Feature001]
  Origin = -> Origin008
  Placement = pos=(127.21,-130.36,-1.6) rot=(-0.57735,0.57735,-0.57735;2.0944rad)
FEATURE [App::Link] J2_CUI_DEVICES_TB001_500_P04GR_5FCB9D5E_2__ln_  label="J4_CUI_DEVICES_TB001-500-P04GR_5FA8521F[2]"
  LinkPlacement = pos=(160.325,-130.7,-1.6) rot=(-1,0,0;1.5708rad)
  LinkedObject = -> CUI_DEVICES_TB001_500_P04GR
  Placement = pos=(160.325,-130.7,-1.6) rot=(-1,0,0;1.5708rad)
FEATURE [Part::Feature] Shape009  label="J1_usb_b_conn_5FA8DFDA[2]"
  Placement = pos=(161.05,-89.5,-1.6) rot=(1,0,0;3.14159rad)
  shape: bbox 16.5 x 14.34 x 14.52 mm, 44 faces (baked)
FEATURE [Part::Feature] Shape010  label="U1_SSOP_28_53x102mm_P065mm_5FB0862F"
  Placement = pos=(145.91,-85.68,-1.6) rot=(1,0,0;3.14159rad)
  shape: bbox 7.8 x 10.2 x 2.1 mm, 456 faces (baked)
FEATURE [Part::Feature] Shape011  label="Y1_Crystal_5F93F8CD"
  Placement = pos=(129.46,-134.77,0) rot=(0,0,1;3.14159rad)
  shape: bbox 11.35 x 5 x 16.4 mm, 15 faces (baked)
FEATURE [Part::Feature] Shape012  label="U2_DIP-28_W7.62mm_5F8B1761"
  Placement = pos=(108,-126.4,0) rot=(0,0,1;1.5708rad)
  shape: bbox 35.56 x 7.874 x 6.98 mm, 488 faces (baked)
FEATURE [Part::Feature] Shape013  label="J3_PinSocket_1x16_P254mm_Vertical_5FB99047"
  Placement = pos=(97,-88.5,0) rot=(0,0,1;1.5708rad)
  shape: bbox 40.64 x 2.54 x 10.1 mm, 506 faces (baked)
FEATURE [Part::Feature] Shape014  label="J5_PinHeader_2x03_P254mm_Vertical_5FA86B0F"
  Placement = pos=(123.69,-110.005,-1.6) rot=(0.707107,0.707107,0;3.14159rad)
  shape: bbox 7.62 x 5.08 x 11.54 mm, 130 faces (baked)
FEATURE [App::Part] Bot_8929
  Group = -> [Shape,Shape002,Shape006,CUI_DEVICES_TB001_500_P04GR,J2_CUI_DEVICES_TB001_500_P04GR_5FCB9D5E_2__ln_,Shape009,Shape010,Shape014]
  Origin = -> Origin004
FEATURE [App::Link] C5_C_Disc_D50mm_W25mm_P250mm_5FB07593_ln_  label="C1_C_Disc_D50mm_W25mm_P250mm_5FA6C044"
  LinkPlacement = pos=(156.15,-88.02,0) rot=(0,0,1;1.5708rad)
  LinkedObject = -> Shape008
  Placement = pos=(156.15,-88.02,0) rot=(0,0,1;1.5708rad)
FEATURE [App::Link] C5_C_Disc_D50mm_W25mm_P250mm_5FB07593_ln_001  label="C2_C_Disc_D50mm_W25mm_P250mm_5FAFE4E7"
  LinkPlacement = pos=(152.68,-85.53,0) rot=(0,0,-1;1.5708rad)
  LinkedObject = -> Shape008
  Placement = pos=(152.68,-85.53,0) rot=(0,0,-1;1.5708rad)
FEATURE [App::Link] C5_C_Disc_D50mm_W25mm_P250mm_5FB07593_ln_002  label="C3_C_Disc_D50mm_W25mm_P250mm_5FA6C068"
  LinkPlacement = pos=(125.62,-116,0) rot=(0,0,1;3.14159rad)
  LinkedObject = -> Shape008
  Placement = pos=(125.62,-116,0) rot=(0,0,1;3.14159rad)
FEATURE [App::Link] C5_C_Disc_D50mm_W25mm_P250mm_5FB07593_ln_003  label="C4_C_Disc_D50mm_W25mm_P250mm_5FCE6386"
  LinkPlacement = pos=(92.11,-128.56,0) rot=(0,0,1;1.5708rad)
  LinkedObject = -> Shape008
  Placement = pos=(92.11,-128.56,0) rot=(0,0,1;1.5708rad)
FEATURE [App::Link] C5_C_Disc_D50mm_W25mm_P250mm_5FB07593_ln_004  label="C6_C_Disc_D50mm_W25mm_P250mm_5FA6D61D"
  LinkPlacement = pos=(128.67,-116,0) rot=(0,0,1;0rad)
  LinkedObject = -> Shape008
  Placement = pos=(128.67,-116,0) rot=(0,0,1;0rad)
FEATURE [App::Link] C5_C_Disc_D50mm_W25mm_P250mm_5FB07593_ln_005  label="C7_C_Disc_D50mm_W25mm_P250mm_5FA6C09E"
  LinkPlacement = pos=(121.8,-136.3,0) rot=(0,0,1;1.5708rad)
  LinkedObject = -> Shape008
  Placement = pos=(121.8,-136.3,0) rot=(0,0,1;1.5708rad)
FEATURE [App::Link] C5_C_Disc_D50mm_W25mm_P250mm_5FB07593_ln_006  label="C8_C_Disc_D50mm_W25mm_P250mm_5FA6C0B0"
  LinkPlacement = pos=(137.15,-136.3,0) rot=(0,0,1;1.5708rad)
  LinkedObject = -> Shape008
  Placement = pos=(137.15,-136.3,0) rot=(0,0,1;1.5708rad)
FEATURE [App::Link] D4_LED_D5_0mm_5FA6C0E4_ln_  label="D1_LED_D5.0mm_5FCBACB3"
  LinkPlacement = pos=(135.2,-73.4,0) rot=(0,0,1;0rad)
  LinkedObject = -> Shape004
  Placement = pos=(135.2,-73.4,0) rot=(0,0,1;0rad)
FEATURE [App::Link] D4_LED_D5_0mm_5FA6C0E4_ln_001  label="D2_LED_D5.0mm_5FCBAF12"
  LinkPlacement = pos=(141.9,-73.4,0) rot=(0,0,1;0rad)
  LinkedObject = -> Shape004
  Placement = pos=(141.9,-73.4,0) rot=(0,0,1;0rad)
FEATURE [Part::Feature] Shape015  label="R1_R_Axial_DIN0309_L90mm_D32mm_P1270mm_Horizontal_5FCA8AFD"
  Placement = pos=(109.85,-103.11,0) rot=(0,0,1;0rad)
  shape: bbox 13.63 x 3.464 x 6.332 mm, 17 faces (baked)
FEATURE [App::Link] R1_R_Axial_DIN0309_L90mm_D32mm_P1270mm_Horizontal_5FCA8AFD_ln_  label="R2_R_Axial_DIN0309_L90mm_D32mm_P1270mm_Horizontal_5FCA8ABB"
  LinkPlacement = pos=(109.85,-99.065,0) rot=(0,0,1;0rad)
  LinkedObject = -> Shape015
  Placement = pos=(109.85,-99.065,0) rot=(0,0,1;0rad)
FEATURE [App::Link] R1_R_Axial_DIN0309_L90mm_D32mm_P1270mm_Horizontal_5FCA8AFD_ln_001  label="R3_R_Axial_DIN0309_L90mm_D32mm_P1270mm_Horizontal_5FB070BF"
  LinkPlacement = pos=(130.875,-105.765,0) rot=(0,0,1;1.5708rad)
  LinkedObject = -> Shape015
  Placement = pos=(130.875,-105.765,0) rot=(0,0,1;1.5708rad)
FEATURE [App::Link] R1_R_Axial_DIN0309_L90mm_D32mm_P1270mm_Horizontal_5FCA8AFD_ln_002  label="R4_R_Axial_DIN0309_L90mm_D32mm_P1270mm_Horizontal_5FB0707D"
  LinkPlacement = pos=(134.875,-105.765,0) rot=(0,0,1;1.5708rad)
  LinkedObject = -> Shape015
  Placement = pos=(134.875,-105.765,0) rot=(0,0,1;1.5708rad)
FEATURE [App::Link] R1_R_Axial_DIN0309_L90mm_D32mm_P1270mm_Horizontal_5FCA8AFD_ln_003  label="R6_R_Axial_DIN0309_L90mm_D32mm_P1270mm_Horizontal_5FA6C1B1"
  LinkPlacement = pos=(111.3,-133.7,0) rot=(0,0,1;3.14159rad)
  LinkedObject = -> Shape015
  Placement = pos=(111.3,-133.7,0) rot=(0,0,1;3.14159rad)
FEATURE [App::Link] R1_R_Axial_DIN0309_L90mm_D32mm_P1270mm_Horizontal_5FCA8AFD_ln_004  label="R7_R_Axial_DIN0309_L90mm_D32mm_P1270mm_Horizontal_5FA6CB65"
  LinkPlacement = pos=(123.1,-129.75,0) rot=(0,0,1;0rad)
  LinkedObject = -> Shape015
  Placement = pos=(123.1,-129.75,0) rot=(0,0,1;0rad)
FEATURE [App::Link] R1_R_Axial_DIN0309_L90mm_D32mm_P1270mm_Horizontal_5FCA8AFD_ln_005  label="R8_R_Axial_DIN0309_L90mm_D32mm_P1270mm_Horizontal_5FA6F1A2"
  LinkPlacement = pos=(147.31,-122.925,0) rot=(0,0,1;0rad)
  LinkedObject = -> Shape015
  Placement = pos=(147.31,-122.925,0) rot=(0,0,1;0rad)
FEATURE [App::Link] R1_R_Axial_DIN0309_L90mm_D32mm_P1270mm_Horizontal_5FCA8AFD_ln_006  label="R9_R_Axial_DIN0309_L90mm_D32mm_P1270mm_Horizontal_5FB07101"
  LinkPlacement = pos=(138.875,-93.065,0) rot=(0,0,-1;1.5708rad)
  LinkedObject = -> Shape015
  Placement = pos=(138.875,-93.065,0) rot=(0,0,-1;1.5708rad)
FEATURE [App::Link] R1_R_Axial_DIN0309_L90mm_D32mm_P1270mm_Horizontal_5FCA8AFD_ln_007  label="R11_R_Axial_DIN0309_L90mm_D32mm_P1270mm_Horizontal_5FCB9A34"
  LinkPlacement = pos=(160.01,-126.73,0) rot=(0,0,1;3.14159rad)
  LinkedObject = -> Shape015
  Placement = pos=(160.01,-126.73,0) rot=(0,0,1;3.14159rad)
FEATURE [App::Part] Top_8929
  Group = -> [Shape001,Shape003,RV1_ACP470_5F3BE09B_ln_,Shape004,Shape005,F1_MF_MSMF050_5FB19120_2__ln_,Shape007,Shape008,Shape011,Shape012,Shape013,C5_C_Disc_D50mm_W25mm_P250mm_5FB07593_ln_,C5_C_Disc_D50mm_W25mm_P250mm_5FB07593_ln_001,C5_C_Disc_D50mm_W25mm_P250mm_5FB07593_ln_002,C5_C_Disc_D50mm_W25mm_P250mm_5FB07593_ln_003,C5_C_Disc_D50mm_W25mm_P250mm_5FB07593_ln_004,+13 more]
  Origin = -> Origin003
FEATURE [App::Part] Step_Models_8929
  Group = -> [Top_8929,Bot_8929]
  Origin = -> Origin002
FEATURE [PartDesign::CoordinateSystem] LCS_lcd
  AttacherType = Attacher::AttachEngine3D
  MapMode = 7
  Placement = pos=(95.73,-87.23,7) rot=(0,0.707107,0.707107;3.14159rad)
  Support = -> [Shape013]
FEATURE [PartDesign::CoordinateSystem] LCS_box
  AttacherType = Attacher::AttachEngine3D
  MapMode = 11
  Placement = pos=(93,-134,-1.6) rot=(0,0,1;1.5708rad)
  Support = -> [Pcb_8929]
FEATURE [App::Part] Board_8929  label="livello_serbatoio_definitiva"
  Group = -> [Board_Geoms_8929,Step_Models_8929,LCS_lcd,LCS_box]
  Origin = -> Origin001
---- part push_button.FCStd = doc fcstd_784a89f978fb ----
FCSTD DOCUMENT  (FreeCAD 0.19R22665 (Git))
Label: push_button
License: All rights reserved
LicenseURL: http://en.wikipedia.org/wiki/All_rights_reserved
objects: Sketcher::SketchObject×5, PartDesign::Pad×4, PartDesign::Pocket×1, PartDesign::Body×1, Part::Box×1, Part::Fuse×1, PartDesign::CoordinateSystem×1, App::Part×1
note: 19 computed .brp shape members not serialized (recipe doc carries the construction recipe); baked Part::Feature solids carry a one-line shape summary decoded from their .brp

FEATURE [Sketcher::SketchObject] Sketch
  MapMode = 5
  Placement = pos=(0,0,0) rot=(1,0,0;1.5708rad)
  Support = -> [XZ_Plane]
  sketch-geometry (1):
    g0: Circle CenterX=0 CenterY=0 CenterZ=0 NormalX=0 NormalY=0 NormalZ=1 AngleXU=0 Radius=11
  constraints (2):
    c: Coincident(g0,g-1)
    c: Diameter(g0) = 22
FEATURE [PartDesign::Pad] Pad
  Direction = (1,1,1)
  Length = 2
  Length2 = 100
  Placement = pos=(0,0,0) rot=(1,0,0;1.5708rad)
  Profile = -> Sketch
  Type = 0
FEATURE [Sketcher::SketchObject] Sketch001
  ExternalGeometry = -> [Pad]
  MapMode = 5
  Placement = pos=(0,0,0) rot=(-1,0,0;1.5708rad)
  Support = -> [Pad]
  sketch-geometry (1):
    g0: Circle CenterX=0 CenterY=0 CenterZ=0 NormalX=0 NormalY=0 NormalZ=1 AngleXU=0 Radius=9.5
  constraints (2):
    c: Coincident(g0,g-1)
    c: Diameter(g0) = 19
FEATURE [PartDesign::Pad] Pad001
  BaseFeature = -> Pad
  Direction = (1,1,1)
  Length = 15
  Length2 = 100
  Placement = pos=(0,0,0) rot=(1,0,0;1.5708rad)
  Profile = -> Sketch001
  Type = 0
FEATURE [Sketcher::SketchObject] Sketch002
  ExternalGeometry = -> [Pad001]
  MapMode = 5
  Placement = pos=(0,15,-6.6e-15) rot=(-1,0,0;1.5708rad)
  Support = -> [Pad001]
  sketch-geometry (1):
    g0: Circle CenterX=0 CenterY=0 CenterZ=0 NormalX=0 NormalY=0 NormalZ=1 AngleXU=0 Radius=9.25
  constraints (2):
    c: Coincident(g0,g-1)
    c: Diameter(g0) = 18.5
FEATURE [PartDesign::Pad] Pad002
  BaseFeature = -> Pad001
  Direction = (1,1,1)
  Length = 23
  Length2 = 100
  Placement = pos=(0,0,0) rot=(1,0,0;1.5708rad)
  Profile = -> Sketch002
  Type = 0
FEATURE [Sketcher::SketchObject] Sketch003
  MapMode = 5
  Placement = pos=(0,-2,4e-16) rot=(1,0,0;1.5708rad)
  Support = -> [Pad002]
  sketch-geometry (1):
    g0: Circle CenterX=0 CenterY=0 CenterZ=0 NormalX=0 NormalY=0 NormalZ=1 AngleXU=0 Radius=8.5
  constraints (2):
    c: Coincident(g0,g-1)
    c: Diameter(g0) = 17
FEATURE [PartDesign::Pocket] Pocket
  BaseFeature = -> Pad002
  Length = 2
  Length2 = 100
  Placement = pos=(0,0,0) rot=(1,0,0;1.5708rad)
  Profile = -> Sketch003
  Type = 0
FEATURE [Sketcher::SketchObject] Sketch004
  ExternalGeometry = -> [Pocket]
  MapMode = 5
  Placement = pos=(0,0,0) rot=(1,0,0;1.5708rad)
  Support = -> [Pocket]
  sketch-geometry (1):
    g0: Circle CenterX=0 CenterY=0 CenterZ=0 NormalX=0 NormalY=0 NormalZ=1 AngleXU=0 Radius=7.5
  constraints (2):
    c: Coincident(g0,g-1)
    c: Diameter(g0) = 15
FEATURE [PartDesign::Pad] Pad003
  BaseFeature = -> Pocket
  Direction = (1,1,1)
  Length = 2
  Length2 = 100
  Placement = pos=(0,0,0) rot=(1,0,0;1.5708rad)
  Profile = -> Sketch004
  Type = 0
FEATURE [PartDesign::Body] Body  label="button"
  Group = -> [Sketch,Pad,Sketch001,Pad001,Sketch002,Pad002,Sketch003,Pocket,Sketch004,Pad003]
  Origin = -> Origin
  Tip = -> Pad003
FEATURE [Part::Box] Box  label="Cubo"
  AttacherType = Attacher::AttachEngine3D
  Height = 3
  Length = 8
  Placement = pos=(-4,15,8) rot=(0,0,1;0rad)
  Width = 15
FEATURE [Part::Fuse] Fusion
  Base = -> Body
  Tool = -> Box
FEATURE [PartDesign::CoordinateSystem] LCS_coperchio
  AttacherType = Attacher::AttachEngine3D
  MapMode = 11
  Placement = pos=(0,0,0) rot=(0.57735,-0.57735,-0.57735;4.18879rad)
  Support = -> [Fusion]
FEATURE [App::Part] Part  label="push_button_complete"
  Group = -> [Body,Box,Fusion,LCS_coperchio]
  Origin = -> Origin001
